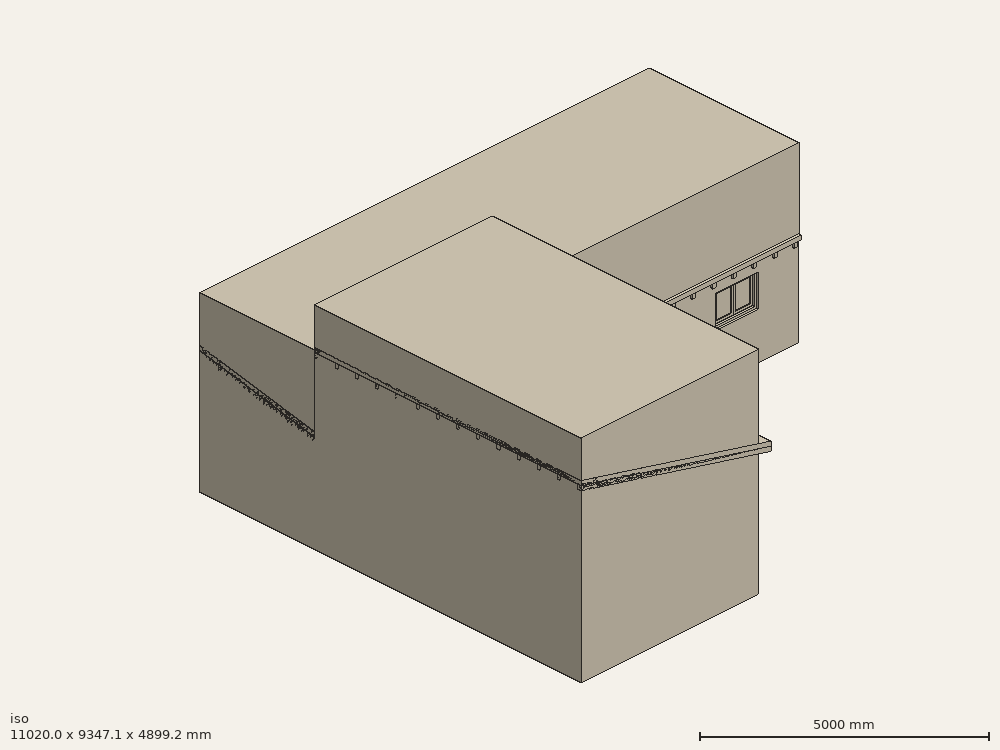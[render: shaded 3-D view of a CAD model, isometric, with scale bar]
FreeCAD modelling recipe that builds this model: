
FCSTD DOCUMENT  (FreeCAD 0.16R5653 (Git))
Label: Maison
License: All rights reserved
LicenseURL: http://en.wikipedia.org/wiki/All_rights_reserved
objects: Part::FeaturePython×87, Part::Part2DObjectPython×74, Sketcher::SketchObject×24, Part::Feature×17, Part::Extrusion×17, Part::MultiCommon×10, Part::Box×8, App::DocumentObjectGroupPython×5, App::DocumentObjectGroup×3, Part::Cut×2, App::FeaturePython×2, Part::Sweep×1, Part::Cylinder×1, Mesh::Feature×1, Mesh::FeaturePython×1
note: 243 computed .brp shape members not serialized (recipe doc carries the construction recipe); baked Part::Feature solids carry a one-line shape summary decoded from their .brp

FEATURE [Sketcher::SketchObject] Sketch001
  expr: Constraints[116] = Constraints.Cloison
  expr: Constraints[118] = Constraints.Cloison
  expr: Constraints[107] = Constraints.Cloison
  expr: Constraints[60] = Constraints.Cloison
  expr: Constraints[105] = Constraints.Cloison
  expr: Constraints[91] = Constraints.Cloison
  expr: Constraints[74] = Constraints.Cloison
  expr: Constraints[75] = Constraints.Cloison
  expr: Constraints[61] = Constraints.Cloison
  sketch-geometry (35):
    g0: LineSegment StartX=200 StartY=9007.1 StartZ=0 EndX=200 EndY=200 EndZ=0
    g1: LineSegment StartX=200 StartY=200 StartZ=0 EndX=4020 EndY=200 EndZ=0
    g2: LineSegment StartX=4020 StartY=200 StartZ=0 EndX=4020 EndY=5877.1 EndZ=0
    g3: LineSegment StartX=4020 StartY=5877.1 StartZ=0 EndX=10680 EndY=5877.1 EndZ=0
    g4: LineSegment StartX=10680 StartY=5877.1 StartZ=0 EndX=10680 EndY=9007.1 EndZ=0
    g5: LineSegment StartX=10680 StartY=9007.1 StartZ=0 EndX=200 EndY=9007.1 EndZ=0
    g6: LineSegment StartX=7960 StartY=5877.1 StartZ=0 EndX=7960 EndY=9007.1 EndZ=0
    g7: LineSegment StartX=7960 StartY=8107.1 StartZ=0 EndX=4020 EndY=8107.1 EndZ=0
    g8: LineSegment StartX=4020 StartY=8107.1 StartZ=0 EndX=4020 EndY=5877.1 EndZ=0
    g9: LineSegment StartX=3090 StartY=9007.1 StartZ=0 EndX=3090 EndY=7247.1 EndZ=0
    g10: LineSegment StartX=3090 StartY=7247.1 StartZ=0 EndX=200 EndY=7247.1 EndZ=0
    g11: LineSegment StartX=5140 StartY=8107.1 StartZ=0 EndX=5140 EndY=5877.1 EndZ=0
    g12: LineSegment StartX=4020 StartY=7327.1 StartZ=0 EndX=5140 EndY=7327.1 EndZ=0
    g13: LineSegment StartX=4580 StartY=8037.1 StartZ=0 EndX=4580 EndY=7327.1 EndZ=0
    g14: LineSegment StartX=4650 StartY=8037.1 StartZ=0 EndX=4650 EndY=7327.1 EndZ=0
    g15: LineSegment StartX=5210 StartY=8107.1 StartZ=0 EndX=5210 EndY=5877.1 EndZ=0
    g16: LineSegment StartX=8030 StartY=9007.1 StartZ=0 EndX=8030 EndY=5877.1 EndZ=0
    g17: LineSegment StartX=4020 StartY=8037.1 StartZ=0 EndX=5140 EndY=8037.1 EndZ=0
    g18: LineSegment StartX=200 StartY=5090 StartZ=0 EndX=2110 EndY=5090 EndZ=0
    g19: LineSegment StartX=2110 StartY=5090 StartZ=0 EndX=2560 EndY=5810 EndZ=0
    g20: LineSegment StartX=4090 StartY=7257.1 StartZ=0 EndX=5140 EndY=7257.1 EndZ=0
    g21: LineSegment StartX=4330 StartY=5877.1 StartZ=0 EndX=4330 EndY=6557.1 EndZ=0
    g22: LineSegment StartX=4330 StartY=6557.1 StartZ=0 EndX=4090 EndY=6557.1 EndZ=0
    g23: LineSegment StartX=4090 StartY=6557.1 StartZ=0 EndX=4090 EndY=7257.1 EndZ=0
    g24: LineSegment StartX=4090 StartY=7327.1 StartZ=0 EndX=4090 EndY=8037.1 EndZ=0
    g25: LineSegment StartX=5210 StartY=8037.1 StartZ=0 EndX=7960 EndY=8037.1 EndZ=0
    g26: LineSegment StartX=3160 StartY=9007.1 StartZ=0 EndX=3160 EndY=6307.1 EndZ=0
    g27: LineSegment StartX=3160 StartY=6307.1 StartZ=0 EndX=3090 EndY=6307.1 EndZ=0
    g28: LineSegment StartX=3090 StartY=6307.1 StartZ=0 EndX=3090 EndY=7177.1 EndZ=0
    g29: LineSegment StartX=3090 StartY=7177.1 StartZ=0 EndX=200 EndY=7177.1 EndZ=0
    g30: LineSegment StartX=1520 StartY=7247.1 StartZ=0 EndX=1520 EndY=9007.1 EndZ=0
    g31: LineSegment StartX=1590 StartY=7247.1 StartZ=0 EndX=1590 EndY=9007.1 EndZ=0
    g32: LineSegment StartX=200 StartY=5160 StartZ=0 EndX=2071.2 EndY=5160 EndZ=0
    g33: LineSegment StartX=2071.2 StartY=5160 StartZ=0 EndX=2500.64 EndY=5847.1 EndZ=0
    g34: LineSegment StartX=2500.64 StartY=5847.1 StartZ=0 EndX=2560 EndY=5810 EndZ=0
  constraints (123):
    c: Vertical(g0)
    c: Coincident(g0,g1)
    c: Horizontal(g1)
    c: Coincident(g1,g2)
    c: Vertical(g2)
    c: Coincident(g2,g3)
    c: Horizontal(g3)
    c: Coincident(g3,g4)
    c: Vertical(g4)
    c: Coincident(g4,g5)
    c: Coincident(g5,g0)
    c: Horizontal(g5)
    c: PointOnObject(g6,g3)
    c: PointOnObject(g6,g5)
    c: Vertical(g6)
    c: PointOnObject(g7,g6)
    c: Horizontal(g7)
    c: Coincident(g8,g7)
    c: Vertical(g8)
    c: Coincident(g8,g2)
    c: PointOnObject(g9,g5)
    c: Vertical(g9)
    c: Coincident(g9,g10)
    c: PointOnObject(g10,g0)
    c: Horizontal(g10)
    c: PointOnObject(g11,g7)
    c: PointOnObject(g11,g3)
    c: Vertical(g11)
    c: PointOnObject(g12,g8)
    c: PointOnObject(g12,g11)
    c: Horizontal(g12)
    c: PointOnObject(g13,g12)
    c: Vertical(g13)
    c: PointOnObject(g14,g12)
    c: Vertical(g14)
    c: PointOnObject(g15,g7)
    c: PointOnObject(g15,g3)
    c: Vertical(g15)
    c: PointOnObject(g16,g5)
    c: PointOnObject(g16,g3)
    c: Vertical(g16)
    c: PointOnObject(g17,g8)
    c: PointOnObject(g17,g11)
    c: Horizontal(g17)
    c: PointOnObject(g13,g17)
    c: PointOnObject(g14,g17)
    c: DistanceX(g1) = 3820
    c: PointOnObject(g18,g0)
    c: Horizontal(g18)
    c: Coincident(g18,g19)
    c: DistanceX(g18) = 1910
    c: DistanceX(g19) = 450
    c: DistanceY(g19) = 720
    c: DistanceY(g0,g18) = 4890
    c: DistanceX(g16,g4) = 2650
    c: DistanceY(g4) = 3130
    c: DistanceY(g6,g7) = -900
    c: DistanceX(g6,g16) = 70  'Cloison'
    c: DistanceX(g15,g7) = 2750
    c: DistanceX(g11,g15) = 70
    c: DistanceY(g17,g7) = 70
    c: DistanceX(g13,g14) = 70
    c: PointOnObject(g20,g11)
    c: Horizontal(g20)
    c: DistanceX(g20) = 1050
    c: PointOnObject(g21,g3)
    c: Vertical(g21)
    c: DistanceX(g21,g11) = 810
    c: DistanceY(g13) = -710
    c: Coincident(g21,g22)
    c: Horizontal(g22)
    c: Coincident(g22,g23)
    c: Coincident(g23,g20)
    c: Vertical(g23)
    c: DistanceX(g12,g20) = 70
    c: DistanceY(g20,g12) = 70
    c: DistanceY(g21,g21) = 680
    c: PointOnObject(g24,g12)
    c: PointOnObject(g24,g17)
    c: Vertical(g24)
    c: PointOnObject(g24,g23)
    c: DistanceX(g24,g17) = 1050
    c: DistanceX(g14,g17) = 490
    c: DistanceX(g24,g13) = 490
    c: PointOnObject(g25,g15)
    c: PointOnObject(g25,g6)
    c: Horizontal(g25)
    c: PointOnObject(g25,g17)
    c: PointOnObject(g26,g5)
    c: Vertical(g26)
    c: DistanceX(g26,g7) = 860
    c: DistanceX(g9,g26) = 70
    c: Coincident(g26,g27)
    c: Horizontal(g27)
    c: Coincident(g27,g28)
    c: Vertical(g28)
    c: Coincident(g28,g29)
    c: PointOnObject(g29,g0)
    c: Horizontal(g29)
    c: PointOnObject(g30,g10)
    c: PointOnObject(g30,g5)
    c: PointOnObject(g31,g10)
    c: PointOnObject(g31,g5)
    c: Vertical(g31)
    c: Vertical(g30)
    c: DistanceX(g30,g31) = 70
    c: PointOnObject(g28,g9)
    c: DistanceY(g29,g10) = 70
    c: DistanceY(g9,g9) = 1760
    c: DistanceX(g31,g9) = 1500
    c: DistanceY(g27,g28) = 870
    c: PointOnObject(g32,g0)
    c: Horizontal(g32)
    c: Coincident(g32,g33)
    c: Coincident(g33,g34)
    c: Coincident(g34,g19)
    c: Distance(g34) = 70
    c: Parallel(g33,g19)
    c: DistanceY(g18,g32) = 70
    c: Perpendicular(g34,g19)
    c: DistanceX(g0) = 200
    c: DistanceY(g0) = 200
    c: DistanceY(g33,g27) = 460
FEATURE [Sketcher::SketchObject] TraceDuMur
  sketch-geometry (1):
    g0: LineSegment StartX=8030 StartY=5877.1 StartZ=0 EndX=8030 EndY=9007.1 EndZ=0
FEATURE [Sketcher::SketchObject] TraceDuMur001
  sketch-geometry (1):
    g0: LineSegment StartX=7960 StartY=8037.1 StartZ=0 EndX=4020 EndY=8037.1 EndZ=0
FEATURE [Part::FeaturePython] Wall001  label="Cloison"  # WARN: FeaturePython — macro-defined, semantics opaque (R4)
  Align = 0
  Base = -> TraceDuMur001
  Face = 0
  Height = 3000
  Length = 0
  MoveWithHost = false
  Normal = (0,0,0)
  Role = 0
  Width = 70
FEATURE [Sketcher::SketchObject] TraceDuMur002
  sketch-geometry (1):
    g0: LineSegment StartX=5210 StartY=8037.1 StartZ=0 EndX=5210 EndY=5877.1 EndZ=0
FEATURE [Part::FeaturePython] Wall002  label="Cloison001"  # WARN: FeaturePython — macro-defined, semantics opaque (R4)
  Align = 0
  Base = -> TraceDuMur002
  Face = 0
  Height = 3000
  Length = 0
  MoveWithHost = false
  Normal = (0,0,0)
  Role = 0
  Width = 70
FEATURE [Sketcher::SketchObject] TraceDuMur003
  sketch-geometry (1):
    g0: LineSegment StartX=4090 StartY=8037.1 StartZ=0 EndX=4090 EndY=6557.1 EndZ=0
FEATURE [Part::FeaturePython] Wall003  label="Cloison004"  # WARN: FeaturePython — macro-defined, semantics opaque (R4)
  Align = 0
  Base = -> TraceDuMur003
  Face = 0
  Height = 3000
  Length = 0
  MoveWithHost = false
  Normal = (0,0,0)
  Role = 0
  Width = 70
FEATURE [Sketcher::SketchObject] TraceDuMur004
  sketch-geometry (1):
    g0: LineSegment StartX=4650 StartY=8037.1 StartZ=0 EndX=4650 EndY=7327.1 EndZ=0
FEATURE [Part::FeaturePython] Wall004  label="Cloison003"  # WARN: FeaturePython — macro-defined, semantics opaque (R4)
  Align = 0
  Base = -> TraceDuMur004
  Face = 0
  Height = 3000
  Length = 0
  MoveWithHost = false
  Normal = (0,0,0)
  Role = 0
  Width = 70
FEATURE [Sketcher::SketchObject] TraceDuMur005
  sketch-geometry (1):
    g0: LineSegment StartX=5140 StartY=7257.1 StartZ=0 EndX=4090 EndY=7257.1 EndZ=0
FEATURE [Part::FeaturePython] Wall005  label="Cloison002"  # WARN: FeaturePython — macro-defined, semantics opaque (R4)
  Align = 0
  Base = -> TraceDuMur005
  Face = 0
  Height = 3000
  Length = 0
  MoveWithHost = false
  Normal = (0,0,0)
  Role = 0
  Width = 70
FEATURE [Part::Part2DObjectPython] Line  # Draft 2D object (typed FeaturePython)
  ChamferSize = 0
  Closed = false
  End = (3160,6307.1,0)
  FilletRadius = 0
  Length = 2700
  MakeFace = false
  Points = (2) [(3160,9007.1,0),(3160,6307.1,0)]
  Start = (3160,9007.1,0)
FEATURE [Part::Part2DObjectPython] Line001  # Draft 2D object (typed FeaturePython)
  ChamferSize = 0
  Closed = false
  End = (200,7177.1,0)
  FilletRadius = 0
  Length = 2890
  MakeFace = false
  Points = (2) [(3090,7177.1,0),(200,7177.1,0)]
  Start = (3090,7177.1,0)
FEATURE [Part::Part2DObjectPython] Line002  # Draft 2D object (typed FeaturePython)
  ChamferSize = 0
  Closed = false
  End = (1590,7247.1,0)
  FilletRadius = 0
  Length = 1760
  MakeFace = false
  Points = (2) [(1590,9007.1,0),(1590,7247.1,0)]
  Start = (1590,9007.1,0)
FEATURE [Part::FeaturePython] Wall007  label="Cloison005"  # WARN: FeaturePython — macro-defined, semantics opaque (R4)
  Align = 0
  Base = -> Line001
  Face = 0
  Height = 3000
  Length = 0
  MoveWithHost = false
  Normal = (0,0,0)
  Role = 0
  Width = 70
FEATURE [Part::FeaturePython] Wall008  label="Cloison006"  # WARN: FeaturePython — macro-defined, semantics opaque (R4)
  Align = 0
  Base = -> Line002
  Face = 0
  Height = 3000
  Length = 0
  MoveWithHost = false
  Normal = (0,0,0)
  Role = 0
  Width = 70
FEATURE [Part::Part2DObjectPython] DWire  # Draft 2D object (typed FeaturePython)
  ChamferSize = 0
  Closed = true
  End = (200,9007.1,0)
  FilletRadius = 0
  Length = 38574.2
  MakeFace = false
  Points = (6) [(200,200,0),(4020,200,0),(4020,5877.1,0),(10680,5877.1,0),(10680,9007.1,0),(200,9007.1,0)]
  Start = (200,200,0)
FEATURE [Part::Part2DObjectPython] Line003  # Draft 2D object (typed FeaturePython)
  ChamferSize = 0
  Closed = false
  End = (4020,6557.1,0)
  FilletRadius = 0
  Length = 680
  MakeFace = false
  Points = (2) [(4020,5877.1,0),(4020,6557.1,0)]
  Start = (4020,5877.1,0)
FEATURE [Part::Part2DObjectPython] DWire001  # Draft 2D object (typed FeaturePython)
  ChamferSize = 0
  Closed = false
  End = (2560,5810,0)
  FilletRadius = 0
  Length = 2759.06
  MakeFace = false
  Points = (3) [(200,5090,0),(2110,5090,0),(2560,5810,0)]
  Start = (200,5090,0)
FEATURE [Sketcher::SketchObject] Sketch
  Placement = pos=(4290,4307,30) rot=(0.57735,0.57735,0.57735;2.0944rad)
  sketch-geometry (12):
    g0: LineSegment StartX=0 StartY=0 StartZ=0 EndX=900 EndY=0 EndZ=0
    g1: LineSegment StartX=900 StartY=0 StartZ=0 EndX=900 EndY=2150 EndZ=0
    g2: LineSegment StartX=900 StartY=2150 StartZ=0 EndX=0 EndY=2150 EndZ=0
    g3: LineSegment StartX=0 StartY=2150 StartZ=0 EndX=0 EndY=0 EndZ=0
    g4: LineSegment StartX=50 StartY=0 StartZ=0 EndX=850 EndY=0 EndZ=0
    g5: LineSegment StartX=850 StartY=0 StartZ=0 EndX=850 EndY=2100 EndZ=0
    g6: LineSegment StartX=850 StartY=2100 StartZ=0 EndX=50 EndY=2100 EndZ=0
    g7: LineSegment StartX=50 StartY=2100 StartZ=0 EndX=50 EndY=0 EndZ=0
    g8: LineSegment StartX=100 StartY=2050 StartZ=0 EndX=800 EndY=2050 EndZ=0
    g9: LineSegment StartX=800 StartY=2050 StartZ=0 EndX=800 EndY=1200 EndZ=0
    g10: LineSegment StartX=800 StartY=1200 StartZ=0 EndX=100 EndY=1200 EndZ=0
    g11: LineSegment StartX=100 StartY=1200 StartZ=0 EndX=100 EndY=2050 EndZ=0
  constraints (35):
    c: Coincident(g0,g1)
    c: Coincident(g1,g2)
    c: Coincident(g2,g3)
    c: Coincident(g3,g0)
    c: Horizontal(g0)
    c: Horizontal(g2)
    c: Vertical(g1)
    c: Vertical(g3)
    c: Coincident(g4,g5)
    c: Coincident(g5,g6)
    c: Coincident(g6,g7)
    c: Coincident(g7,g4)
    c: Horizontal(g4)
    c: Horizontal(g6)
    c: Vertical(g5)
    c: Vertical(g7)
    c: DistanceY(g1) = 2150
    c: DistanceX(g0) = 900
    c: DistanceY(g6,g2) = 50
    c: DistanceX(g2,g6) = 50
    c: DistanceX(g4,g0) = 50
    c: DistanceY(g0,g4) = 0
    c: Coincident(g0,g-1)
    c: Coincident(g8,g9)
    c: Coincident(g9,g10)
    c: Coincident(g10,g11)
    c: Coincident(g11,g8)
    c: Horizontal(g8)
    c: Horizontal(g10)
    c: Vertical(g9)
    c: Vertical(g11)
    c: DistanceX(g6,g8) = 50
    c: DistanceY(g8,g6) = 50
    c: DistanceX(g8,g5) = 50
    c: DistanceY(g10,g8) = 850
FEATURE [Part::FeaturePython] Window  label="Porte d'entrée"  # WARN: FeaturePython — macro-defined, semantics opaque (R4)
  Base = -> Sketch
  Height = 2150
  HoleDepth = 0
  MoveWithHost = true
  Normal = (-1,0,0)
  Preset = 6
  Role = 1
  Width = 900
  WindowParts = OuterFrame | Frame | Wire0,Wire1 | 50.0 | 50.0 | Door | Solid panel | Wire2,Wire1 | 50.0 | 100.0 | Vitrage | Glass panel | Wire2 | 12.0 | 125.0
FEATURE [Sketcher::SketchObject] Sketch002
  Placement = pos=(4290,1150,900) rot=(0.57735,0.57735,0.57735;2.0944rad)
  sketch-geometry (24):
    g0: LineSegment StartX=0 StartY=0 StartZ=0 EndX=900 EndY=0 EndZ=0
    g1: LineSegment StartX=900 StartY=0 StartZ=0 EndX=900 EndY=1780 EndZ=0
    g2: LineSegment StartX=900 StartY=1780 StartZ=0 EndX=0 EndY=1780 EndZ=0
    g3: LineSegment StartX=0 StartY=1780 StartZ=0 EndX=0 EndY=0 EndZ=0
    g4: LineSegment StartX=50 StartY=50 StartZ=0 EndX=850 EndY=50 EndZ=0
    g5: LineSegment StartX=850 StartY=50 StartZ=0 EndX=850 EndY=1730 EndZ=0
    g6: LineSegment StartX=850 StartY=1730 StartZ=0 EndX=50 EndY=1730 EndZ=0
    g7: LineSegment StartX=50 StartY=1730 StartZ=0 EndX=50 EndY=50 EndZ=0
    g8: LineSegment StartX=55 StartY=55 StartZ=0 EndX=447.5 EndY=55 EndZ=0
    g9: LineSegment StartX=447.5 StartY=55 StartZ=0 EndX=447.5 EndY=1725 EndZ=0
    g10: LineSegment StartX=447.5 StartY=1725 StartZ=0 EndX=55 EndY=1725 EndZ=0
    g11: LineSegment StartX=55 StartY=1725 StartZ=0 EndX=55 EndY=55 EndZ=0
    g12: LineSegment StartX=105 StartY=105 StartZ=0 EndX=397.5 EndY=105 EndZ=0
    g13: LineSegment StartX=397.5 StartY=105 StartZ=0 EndX=397.5 EndY=1675 EndZ=0
    g14: LineSegment StartX=397.5 StartY=1675 StartZ=0 EndX=105 EndY=1675 EndZ=0
    g15: LineSegment StartX=105 StartY=1675 StartZ=0 EndX=105 EndY=105 EndZ=0
    g16: LineSegment StartX=452.5 StartY=55 StartZ=0 EndX=845 EndY=55 EndZ=0
    g17: LineSegment StartX=845 StartY=55 StartZ=0 EndX=845 EndY=1725 EndZ=0
    g18: LineSegment StartX=845 StartY=1725 StartZ=0 EndX=452.5 EndY=1725 EndZ=0
    g19: LineSegment StartX=452.5 StartY=1725 StartZ=0 EndX=452.5 EndY=55 EndZ=0
    g20: LineSegment StartX=502.5 StartY=105 StartZ=0 EndX=795 EndY=105 EndZ=0
    g21: LineSegment StartX=795 StartY=105 StartZ=0 EndX=795 EndY=1675 EndZ=0
    g22: LineSegment StartX=795 StartY=1675 StartZ=0 EndX=502.5 EndY=1675 EndZ=0
    g23: LineSegment StartX=502.5 StartY=1675 StartZ=0 EndX=502.5 EndY=105 EndZ=0
  constraints (71):
    c: Coincident(g0,g1)
    c: Coincident(g1,g2)
    c: Coincident(g2,g3)
    c: Coincident(g3,g0)
    c: Horizontal(g0)
    c: Horizontal(g2)
    c: Vertical(g1)
    c: Vertical(g3)
    c: Coincident(g4,g5)
    c: Coincident(g5,g6)
    c: Coincident(g6,g7)
    c: Coincident(g7,g4)
    c: Horizontal(g4)
    c: Horizontal(g6)
    c: Vertical(g5)
    c: Vertical(g7)
    c: DistanceY(g1) = 1780
    c: DistanceX(g0) = 900
    c: DistanceY(g6,g2) = 50
    c: DistanceX(g2,g6) = 50
    c: DistanceX(g4,g0) = 50
    c: DistanceY(g0,g4) = 50
    c: Coincident(g0,g-1)
    c: Coincident(g8,g9)
    c: Coincident(g9,g10)
    c: Coincident(g10,g11)
    c: Coincident(g11,g8)
    c: Horizontal(g8)
    c: Horizontal(g10)
    c: Vertical(g9)
    c: Vertical(g11)
    c: Coincident(g12,g13)
    c: Coincident(g13,g14)
    c: Coincident(g14,g15)
    c: Coincident(g15,g12)
    c: Horizontal(g12)
    c: Horizontal(g14)
    c: Vertical(g13)
    c: Vertical(g15)
    c: Coincident(g16,g17)
    c: Coincident(g17,g18)
    c: Coincident(g18,g19)
    c: Coincident(g19,g16)
    c: Horizontal(g16)
    c: Horizontal(g18)
    c: Vertical(g17)
    c: Vertical(g19)
    c: Coincident(g20,g21)
    c: Coincident(g21,g22)
    c: Coincident(g22,g23)
    c: Coincident(g23,g20)
    c: Horizontal(g20)
    c: Horizontal(g22)
    c: Vertical(g21)
    c: Vertical(g23)
    c: DistanceY(g8,g12) = 50
    c: DistanceX(g8,g12) = 50
    c: DistanceX(g21,g17) = 50
    c: DistanceY(g21,g17) = 50
    c: DistanceX(g16,g20) = 50
    c: DistanceX(g14,g10) = 50
    c: Equal(g22,g14)
    c: DistanceY(g8,g16) = 0
    c: DistanceY(g10,g18) = 0
    c: DistanceX(g4,g8) = 5
    c: DistanceY(g4,g8) = 5
    c: DistanceX(g6,g18) = -5
    c: DistanceY(g6,g18) = -5
    c: DistanceX(g9,g19) = 5
    c: PointOnObject(g13,g22)
    c: PointOnObject(g20,g12)
FEATURE [Part::FeaturePython] Window001  label="Fenêtre Salon"  # WARN: FeaturePython — macro-defined, semantics opaque (R4)
  Base = -> Sketch002
  Height = 1780
  HoleDepth = 0
  MoveWithHost = true
  Normal = (-1,0,0)
  Preset = 3
  Role = 0
  Width = 900
  WindowParts = OuterFrame | Frame | Wire0,Wire1 | 50.0 | 50.0 | LeftFrame | Frame | Wire2,Wire3 | 50.0 | 100.0 | LeftGlass | Glass panel | Wire3 | 5.0 | 125.0 | RightFrame | Frame | Wire4,Wire5 | 50.0 | 100.0 | RightGlass | Glass panel | Wire5 | 5.0 | 125.0
FEATURE [Sketcher::SketchObject] Sketch003
  Placement = pos=(4450.48,5607.1,1350) rot=(1,0,0;1.5708rad)
  sketch-geometry (16):
    g0: LineSegment StartX=0 StartY=0 StartZ=0 EndX=400 EndY=0 EndZ=0
    g1: LineSegment StartX=400 StartY=0 StartZ=0 EndX=400 EndY=400 EndZ=0
    g2: LineSegment StartX=400 StartY=400 StartZ=0 EndX=0 EndY=400 EndZ=0
    g3: LineSegment StartX=0 StartY=400 StartZ=0 EndX=0 EndY=0 EndZ=0
    g4: LineSegment StartX=50 StartY=50 StartZ=0 EndX=350 EndY=50 EndZ=0
    g5: LineSegment StartX=350 StartY=50 StartZ=0 EndX=350 EndY=350 EndZ=0
    g6: LineSegment StartX=350 StartY=350 StartZ=0 EndX=50 EndY=350 EndZ=0
    g7: LineSegment StartX=50 StartY=350 StartZ=0 EndX=50 EndY=50 EndZ=0
    g8: LineSegment StartX=55 StartY=55 StartZ=0 EndX=345 EndY=55 EndZ=0
    g9: LineSegment StartX=345 StartY=55 StartZ=0 EndX=345 EndY=345 EndZ=0
    g10: LineSegment StartX=345 StartY=345 StartZ=0 EndX=55 EndY=345 EndZ=0
    g11: LineSegment StartX=55 StartY=345 StartZ=0 EndX=55 EndY=55 EndZ=0
    g12: LineSegment StartX=105 StartY=105 StartZ=0 EndX=295 EndY=105 EndZ=0
    g13: LineSegment StartX=295 StartY=105 StartZ=0 EndX=295 EndY=295 EndZ=0
    g14: LineSegment StartX=295 StartY=295 StartZ=0 EndX=105 EndY=295 EndZ=0
    g15: LineSegment StartX=105 StartY=295 StartZ=0 EndX=105 EndY=105 EndZ=0
  constraints (47):
    c: Coincident(g0,g1)
    c: Coincident(g1,g2)
    c: Coincident(g2,g3)
    c: Coincident(g3,g0)
    c: Horizontal(g0)
    c: Horizontal(g2)
    c: Vertical(g1)
    c: Vertical(g3)
    c: Coincident(g4,g5)
    c: Coincident(g5,g6)
    c: Coincident(g6,g7)
    c: Coincident(g7,g4)
    c: Horizontal(g4)
    c: Horizontal(g6)
    c: Vertical(g5)
    c: Vertical(g7)
    c: DistanceY(g1) = 400
    c: DistanceX(g0) = 400
    c: DistanceY(g6,g2) = 50
    c: DistanceX(g2,g6) = 50
    c: DistanceX(g4,g0) = 50
    c: DistanceY(g0,g4) = 50
    c: Coincident(g0,g-1)
    c: Coincident(g8,g9)
    c: Coincident(g9,g10)
    c: Coincident(g10,g11)
    c: Coincident(g11,g8)
    c: Horizontal(g8)
    c: Horizontal(g10)
    c: Vertical(g9)
    c: Vertical(g11)
    c: Coincident(g12,g13)
    c: Coincident(g13,g14)
    c: Coincident(g14,g15)
    c: Coincident(g15,g12)
    c: Horizontal(g12)
    c: Horizontal(g14)
    c: Vertical(g13)
    c: Vertical(g15)
    c: DistanceX(g8,g12) = 50
    c: DistanceY(g8,g12) = 50
    c: DistanceX(g14,g10) = 50
    c: DistanceY(g14,g10) = 50
    c: DistanceX(g4,g8) = 5
    c: DistanceY(g4,g8) = 5
    c: DistanceX(g10,g6) = 5
    c: DistanceY(g10,g6) = 5
FEATURE [Part::FeaturePython] Window002  label="Fenêtre WC"  # WARN: FeaturePython — macro-defined, semantics opaque (R4)
  Base = -> Sketch003
  Height = 400
  HoleDepth = 0
  MoveWithHost = true
  Normal = (0,1,0)
  Preset = 2
  Role = 0
  Width = 400
  WindowParts = OuterFrame | Frame | Wire0,Wire1 | 50.0 | 50.0 | InnerFrame | Frame | Wire2,Wire3 | 50.0 | 100.0 | InnerGlass | Glass panel | Wire3 | 5.0 | 125.0
FEATURE [Sketcher::SketchObject] Sketch004
  Placement = pos=(5914.63,5607.1,1070) rot=(1,0,0;1.5708rad)
  sketch-geometry (24):
    g0: LineSegment StartX=0 StartY=0 StartZ=0 EndX=1050 EndY=0 EndZ=0
    g1: LineSegment StartX=1050 StartY=0 StartZ=0 EndX=1050 EndY=750 EndZ=0
    g2: LineSegment StartX=1050 StartY=750 StartZ=0 EndX=0 EndY=750 EndZ=0
    g3: LineSegment StartX=0 StartY=750 StartZ=0 EndX=0 EndY=0 EndZ=0
    g4: LineSegment StartX=50 StartY=50 StartZ=0 EndX=1000 EndY=50 EndZ=0
    g5: LineSegment StartX=1000 StartY=50 StartZ=0 EndX=1000 EndY=700 EndZ=0
    g6: LineSegment StartX=1000 StartY=700 StartZ=0 EndX=50 EndY=700 EndZ=0
    g7: LineSegment StartX=50 StartY=700 StartZ=0 EndX=50 EndY=50 EndZ=0
    g8: LineSegment StartX=55 StartY=55 StartZ=0 EndX=522.5 EndY=55 EndZ=0
    g9: LineSegment StartX=522.5 StartY=55 StartZ=0 EndX=522.5 EndY=695 EndZ=0
    g10: LineSegment StartX=522.5 StartY=695 StartZ=0 EndX=55 EndY=695 EndZ=0
    g11: LineSegment StartX=55 StartY=695 StartZ=0 EndX=55 EndY=55 EndZ=0
    g12: LineSegment StartX=105 StartY=105 StartZ=0 EndX=472.5 EndY=105 EndZ=0
    g13: LineSegment StartX=472.5 StartY=105 StartZ=0 EndX=472.5 EndY=645 EndZ=0
    g14: LineSegment StartX=472.5 StartY=645 StartZ=0 EndX=105 EndY=645 EndZ=0
    g15: LineSegment StartX=105 StartY=645 StartZ=0 EndX=105 EndY=105 EndZ=0
    g16: LineSegment StartX=527.5 StartY=55 StartZ=0 EndX=995 EndY=55 EndZ=0
    g17: LineSegment StartX=995 StartY=55 StartZ=0 EndX=995 EndY=695 EndZ=0
    g18: LineSegment StartX=995 StartY=695 StartZ=0 EndX=527.5 EndY=695 EndZ=0
    g19: LineSegment StartX=527.5 StartY=695 StartZ=0 EndX=527.5 EndY=55 EndZ=0
    g20: LineSegment StartX=577.5 StartY=105 StartZ=0 EndX=945 EndY=105 EndZ=0
    g21: LineSegment StartX=945 StartY=105 StartZ=0 EndX=945 EndY=645 EndZ=0
    g22: LineSegment StartX=945 StartY=645 StartZ=0 EndX=577.5 EndY=645 EndZ=0
    g23: LineSegment StartX=577.5 StartY=645 StartZ=0 EndX=577.5 EndY=105 EndZ=0
  constraints (71):
    c: Coincident(g0,g1)
    c: Coincident(g1,g2)
    c: Coincident(g2,g3)
    c: Coincident(g3,g0)
    c: Horizontal(g0)
    c: Horizontal(g2)
    c: Vertical(g1)
    c: Vertical(g3)
    c: Coincident(g4,g5)
    c: Coincident(g5,g6)
    c: Coincident(g6,g7)
    c: Coincident(g7,g4)
    c: Horizontal(g4)
    c: Horizontal(g6)
    c: Vertical(g5)
    c: Vertical(g7)
    c: DistanceY(g1) = 750
    c: DistanceX(g0) = 1050
    c: DistanceY(g6,g2) = 50
    c: DistanceX(g2,g6) = 50
    c: DistanceX(g4,g0) = 50
    c: DistanceY(g0,g4) = 50
    c: Coincident(g0,g-1)
    c: Coincident(g8,g9)
    c: Coincident(g9,g10)
    c: Coincident(g10,g11)
    c: Coincident(g11,g8)
    c: Horizontal(g8)
    c: Horizontal(g10)
    c: Vertical(g9)
    c: Vertical(g11)
    c: Coincident(g12,g13)
    c: Coincident(g13,g14)
    c: Coincident(g14,g15)
    c: Coincident(g15,g12)
    c: Horizontal(g12)
    c: Horizontal(g14)
    c: Vertical(g13)
    c: Vertical(g15)
    c: Coincident(g16,g17)
    c: Coincident(g17,g18)
    c: Coincident(g18,g19)
    c: Coincident(g19,g16)
    c: Horizontal(g16)
    c: Horizontal(g18)
    c: Vertical(g17)
    c: Vertical(g19)
    c: Coincident(g20,g21)
    c: Coincident(g21,g22)
    c: Coincident(g22,g23)
    c: Coincident(g23,g20)
    c: Horizontal(g20)
    c: Horizontal(g22)
    c: Vertical(g21)
    c: Vertical(g23)
    c: DistanceY(g8,g12) = 50
    c: DistanceX(g8,g12) = 50
    c: DistanceX(g21,g17) = 50
    c: DistanceY(g21,g17) = 50
    c: DistanceX(g16,g20) = 50
    c: DistanceX(g14,g10) = 50
    c: Equal(g22,g14)
    c: DistanceY(g8,g16) = 0
    c: DistanceY(g10,g18) = 0
    c: DistanceX(g4,g8) = 5
    c: DistanceY(g4,g8) = 5
    c: DistanceX(g6,g18) = -5
    c: DistanceY(g6,g18) = -5
    c: DistanceX(g9,g19) = 5
    c: PointOnObject(g13,g22)
    c: PointOnObject(g20,g12)
FEATURE [Part::FeaturePython] Window003  label="Fenêtre Bureau"  # WARN: FeaturePython — macro-defined, semantics opaque (R4)
  Base = -> Sketch004
  Height = 750
  HoleDepth = 0
  MoveWithHost = true
  Normal = (0,1,0)
  Preset = 3
  Role = 0
  Width = 1050
  WindowParts = <same value as first occurrence — deduplicated (x3 in doc)>
FEATURE [Sketcher::SketchObject] Sketch005
  Placement = pos=(8914.63,5607.1,1070) rot=(1,0,0;1.5708rad)
  sketch-geometry (24):
    g0: LineSegment StartX=0 StartY=0 StartZ=0 EndX=1050 EndY=0 EndZ=0
    g1: LineSegment StartX=1050 StartY=0 StartZ=0 EndX=1050 EndY=750 EndZ=0
    g2: LineSegment StartX=1050 StartY=750 StartZ=0 EndX=0 EndY=750 EndZ=0
    g3: LineSegment StartX=0 StartY=750 StartZ=0 EndX=0 EndY=0 EndZ=0
    g4: LineSegment StartX=50 StartY=50 StartZ=0 EndX=1000 EndY=50 EndZ=0
    g5: LineSegment StartX=1000 StartY=50 StartZ=0 EndX=1000 EndY=700 EndZ=0
    g6: LineSegment StartX=1000 StartY=700 StartZ=0 EndX=50 EndY=700 EndZ=0
    g7: LineSegment StartX=50 StartY=700 StartZ=0 EndX=50 EndY=50 EndZ=0
    g8: LineSegment StartX=55 StartY=55 StartZ=0 EndX=522.5 EndY=55 EndZ=0
    g9: LineSegment StartX=522.5 StartY=55 StartZ=0 EndX=522.5 EndY=695 EndZ=0
    g10: LineSegment StartX=522.5 StartY=695 StartZ=0 EndX=55 EndY=695 EndZ=0
    g11: LineSegment StartX=55 StartY=695 StartZ=0 EndX=55 EndY=55 EndZ=0
    g12: LineSegment StartX=105 StartY=105 StartZ=0 EndX=472.5 EndY=105 EndZ=0
    g13: LineSegment StartX=472.5 StartY=105 StartZ=0 EndX=472.5 EndY=645 EndZ=0
    g14: LineSegment StartX=472.5 StartY=645 StartZ=0 EndX=105 EndY=645 EndZ=0
    g15: LineSegment StartX=105 StartY=645 StartZ=0 EndX=105 EndY=105 EndZ=0
    g16: LineSegment StartX=527.5 StartY=55 StartZ=0 EndX=995 EndY=55 EndZ=0
    g17: LineSegment StartX=995 StartY=55 StartZ=0 EndX=995 EndY=695 EndZ=0
    g18: LineSegment StartX=995 StartY=695 StartZ=0 EndX=527.5 EndY=695 EndZ=0
    g19: LineSegment StartX=527.5 StartY=695 StartZ=0 EndX=527.5 EndY=55 EndZ=0
    g20: LineSegment StartX=577.5 StartY=105 StartZ=0 EndX=945 EndY=105 EndZ=0
    g21: LineSegment StartX=945 StartY=105 StartZ=0 EndX=945 EndY=645 EndZ=0
    g22: LineSegment StartX=945 StartY=645 StartZ=0 EndX=577.5 EndY=645 EndZ=0
    g23: LineSegment StartX=577.5 StartY=645 StartZ=0 EndX=577.5 EndY=105 EndZ=0
  constraints (71):
    c: Coincident(g0,g1)
    c: Coincident(g1,g2)
    c: Coincident(g2,g3)
    c: Coincident(g3,g0)
    c: Horizontal(g0)
    c: Horizontal(g2)
    c: Vertical(g1)
    c: Vertical(g3)
    c: Coincident(g4,g5)
    c: Coincident(g5,g6)
    c: Coincident(g6,g7)
    c: Coincident(g7,g4)
    c: Horizontal(g4)
    c: Horizontal(g6)
    c: Vertical(g5)
    c: Vertical(g7)
    c: DistanceY(g1) = 750
    c: DistanceX(g0) = 1050
    c: DistanceY(g6,g2) = 50
    c: DistanceX(g2,g6) = 50
    c: DistanceX(g4,g0) = 50
    c: DistanceY(g0,g4) = 50
    c: Coincident(g0,g-1)
    c: Coincident(g8,g9)
    c: Coincident(g9,g10)
    c: Coincident(g10,g11)
    c: Coincident(g11,g8)
    c: Horizontal(g8)
    c: Horizontal(g10)
    c: Vertical(g9)
    c: Vertical(g11)
    c: Coincident(g12,g13)
    c: Coincident(g13,g14)
    c: Coincident(g14,g15)
    c: Coincident(g15,g12)
    c: Horizontal(g12)
    c: Horizontal(g14)
    c: Vertical(g13)
    c: Vertical(g15)
    c: Coincident(g16,g17)
    c: Coincident(g17,g18)
    c: Coincident(g18,g19)
    c: Coincident(g19,g16)
    c: Horizontal(g16)
    c: Horizontal(g18)
    c: Vertical(g17)
    c: Vertical(g19)
    c: Coincident(g20,g21)
    c: Coincident(g21,g22)
    c: Coincident(g22,g23)
    c: Coincident(g23,g20)
    c: Horizontal(g20)
    c: Horizontal(g22)
    c: Vertical(g21)
    c: Vertical(g23)
    c: DistanceY(g8,g12) = 50
    c: DistanceX(g8,g12) = 50
    c: DistanceX(g21,g17) = 50
    c: DistanceY(g21,g17) = 50
    c: DistanceX(g16,g20) = 50
    c: DistanceX(g14,g10) = 50
    c: Equal(g22,g14)
    c: DistanceY(g8,g16) = 0
    c: DistanceY(g10,g18) = 0
    c: DistanceX(g4,g8) = 5
    c: DistanceY(g4,g8) = 5
    c: DistanceX(g6,g18) = -5
    c: DistanceY(g6,g18) = -5
    c: DistanceX(g9,g19) = 5
    c: PointOnObject(g13,g22)
    c: PointOnObject(g20,g12)
FEATURE [Part::FeaturePython] Window004  label="Fenêtre Chambre"  # WARN: FeaturePython — macro-defined, semantics opaque (R4)
  Base = -> Sketch005
  Height = 750
  HoleDepth = 0
  MoveWithHost = true
  Normal = (0,1,0)
  Preset = 3
  Role = 0
  Width = 1050
  WindowParts = <same value as first occurrence — deduplicated (x3 in doc)>
FEATURE [Sketcher::SketchObject] Sketch006
  Placement = pos=(8030,8165,0) rot=(0.57735,0.57735,0.57735;2.0944rad)
  sketch-geometry (8):
    g0: LineSegment StartX=0 StartY=0 StartZ=0 EndX=800 EndY=0 EndZ=0
    g1: LineSegment StartX=800 StartY=0 StartZ=0 EndX=800 EndY=2100 EndZ=0
    g2: LineSegment StartX=800 StartY=2100 StartZ=0 EndX=0 EndY=2100 EndZ=0
    g3: LineSegment StartX=0 StartY=2100 StartZ=0 EndX=0 EndY=0 EndZ=0
    g4: LineSegment StartX=50 StartY=0 StartZ=0 EndX=750 EndY=0 EndZ=0
    g5: LineSegment StartX=750 StartY=0 StartZ=0 EndX=750 EndY=2050 EndZ=0
    g6: LineSegment StartX=750 StartY=2050 StartZ=0 EndX=50 EndY=2050 EndZ=0
    g7: LineSegment StartX=50 StartY=2050 StartZ=0 EndX=50 EndY=0 EndZ=0
  constraints (23):
    c: Coincident(g0,g1)
    c: Coincident(g1,g2)
    c: Coincident(g2,g3)
    c: Coincident(g3,g0)
    c: Horizontal(g0)
    c: Horizontal(g2)
    c: Vertical(g1)
    c: Vertical(g3)
    c: Coincident(g4,g5)
    c: Coincident(g5,g6)
    c: Coincident(g6,g7)
    c: Coincident(g7,g4)
    c: Horizontal(g4)
    c: Horizontal(g6)
    c: Vertical(g5)
    c: Vertical(g7)
    c: DistanceY(g1) = 2100
    c: DistanceX(g0) = 800
    c: DistanceY(g6,g2) = 50
    c: DistanceX(g2,g6) = 50
    c: DistanceX(g4,g0) = 50
    c: DistanceY(g0,g4) = 0
    c: Coincident(g0,g-1)
FEATURE [Part::FeaturePython] Window005  label="Porte Intérieure"  # WARN: FeaturePython — macro-defined, semantics opaque (R4)
  Base = -> Sketch006
  Height = 2100
  HoleDepth = 0
  MoveWithHost = true
  Normal = (-1,0,0)
  Preset = 6
  Role = 1
  Width = 800
  WindowParts = OuterFrame | Frame | Wire0,Wire1 | 70.0 | 0.0 | Door | Solid panel | Wire1 | 50.0 | 10.0
FEATURE [Sketcher::SketchObject] Sketch007
  Placement = pos=(5230,8037.1,0) rot=(1,0,0;1.5708rad)
  sketch-geometry (8):
    g0: LineSegment StartX=0 StartY=0 StartZ=0 EndX=800 EndY=0 EndZ=0
    g1: LineSegment StartX=800 StartY=0 StartZ=0 EndX=800 EndY=2100 EndZ=0
    g2: LineSegment StartX=800 StartY=2100 StartZ=0 EndX=0 EndY=2100 EndZ=0
    g3: LineSegment StartX=0 StartY=2100 StartZ=0 EndX=0 EndY=0 EndZ=0
    g4: LineSegment StartX=50 StartY=0 StartZ=0 EndX=750 EndY=0 EndZ=0
    g5: LineSegment StartX=750 StartY=0 StartZ=0 EndX=750 EndY=2050 EndZ=0
    g6: LineSegment StartX=750 StartY=2050 StartZ=0 EndX=50 EndY=2050 EndZ=0
    g7: LineSegment StartX=50 StartY=2050 StartZ=0 EndX=50 EndY=0 EndZ=0
  constraints (23):
    c: Coincident(g0,g1)
    c: Coincident(g1,g2)
    c: Coincident(g2,g3)
    c: Coincident(g3,g0)
    c: Horizontal(g0)
    c: Horizontal(g2)
    c: Vertical(g1)
    c: Vertical(g3)
    c: Coincident(g4,g5)
    c: Coincident(g5,g6)
    c: Coincident(g6,g7)
    c: Coincident(g7,g4)
    c: Horizontal(g4)
    c: Horizontal(g6)
    c: Vertical(g5)
    c: Vertical(g7)
    c: DistanceY(g1) = 2100
    c: DistanceX(g0) = 800
    c: DistanceY(g6,g2) = 50
    c: DistanceX(g2,g6) = 50
    c: DistanceX(g4,g0) = 50
    c: DistanceY(g0,g4) = 0
    c: Coincident(g0,g-1)
FEATURE [Part::FeaturePython] Window006  label="Porte Intérieure001"  # WARN: FeaturePython — macro-defined, semantics opaque (R4)
  Base = -> Sketch007
  Height = 2100
  HoleDepth = 0
  MoveWithHost = true
  Normal = (0,0,0)
  Preset = 6
  Role = 1
  Width = 800
  WindowParts = OuterFrame | Frame | Wire0,Wire1 | 70.0 | 0.0 | Door | Solid panel | Wire1 | 50.0 | 10.0
FEATURE [Sketcher::SketchObject] Sketch008
  Placement = pos=(3090,8957.1,0) rot=(0.57735,-0.57735,-0.57735;2.0944rad)
  sketch-geometry (8):
    g0: LineSegment StartX=0 StartY=0 StartZ=0 EndX=800 EndY=0 EndZ=0
    g1: LineSegment StartX=800 StartY=0 StartZ=0 EndX=800 EndY=2100 EndZ=0
    g2: LineSegment StartX=800 StartY=2100 StartZ=0 EndX=0 EndY=2100 EndZ=0
    g3: LineSegment StartX=0 StartY=2100 StartZ=0 EndX=0 EndY=0 EndZ=0
    g4: LineSegment StartX=50 StartY=0 StartZ=0 EndX=750 EndY=0 EndZ=0
    g5: LineSegment StartX=750 StartY=0 StartZ=0 EndX=750 EndY=2050 EndZ=0
    g6: LineSegment StartX=750 StartY=2050 StartZ=0 EndX=50 EndY=2050 EndZ=0
    g7: LineSegment StartX=50 StartY=2050 StartZ=0 EndX=50 EndY=0 EndZ=0
  constraints (23):
    c: Coincident(g0,g1)
    c: Coincident(g1,g2)
    c: Coincident(g2,g3)
    c: Coincident(g3,g0)
    c: Horizontal(g0)
    c: Horizontal(g2)
    c: Vertical(g1)
    c: Vertical(g3)
    c: Coincident(g4,g5)
    c: Coincident(g5,g6)
    c: Coincident(g6,g7)
    c: Coincident(g7,g4)
    c: Horizontal(g4)
    c: Horizontal(g6)
    c: Vertical(g5)
    c: Vertical(g7)
    c: DistanceY(g1) = 2100
    c: DistanceX(g0) = 800
    c: DistanceY(g6,g2) = 50
    c: DistanceX(g2,g6) = 50
    c: DistanceX(g4,g0) = 50
    c: DistanceY(g0,g4) = 0
    c: Coincident(g0,g-1)
FEATURE [Part::FeaturePython] Window007  label="Porte Intérieure002"  # WARN: FeaturePython — macro-defined, semantics opaque (R4)
  Base = -> Sketch008
  Height = 2100
  HoleDepth = 100
  MoveWithHost = true
  Normal = (0,0,0)
  Preset = 6
  Role = 1
  Width = 800
  WindowParts = OuterFrame | Frame | Wire0,Wire1 | 70.0 | 0.0 | Door | Solid panel | Wire1 | 50.0 | 10.0
FEATURE [Sketcher::SketchObject] Sketch009
  Placement = pos=(250,7177.1,0) rot=(1,0,0;1.5708rad)
  sketch-geometry (8):
    g0: LineSegment StartX=0 StartY=0 StartZ=0 EndX=800 EndY=0 EndZ=0
    g1: LineSegment StartX=800 StartY=0 StartZ=0 EndX=800 EndY=2100 EndZ=0
    g2: LineSegment StartX=800 StartY=2100 StartZ=0 EndX=0 EndY=2100 EndZ=0
    g3: LineSegment StartX=0 StartY=2100 StartZ=0 EndX=0 EndY=0 EndZ=0
    g4: LineSegment StartX=50 StartY=0 StartZ=0 EndX=750 EndY=0 EndZ=0
    g5: LineSegment StartX=750 StartY=0 StartZ=0 EndX=750 EndY=2050 EndZ=0
    g6: LineSegment StartX=750 StartY=2050 StartZ=0 EndX=50 EndY=2050 EndZ=0
    g7: LineSegment StartX=50 StartY=2050 StartZ=0 EndX=50 EndY=0 EndZ=0
  constraints (23):
    c: Coincident(g0,g1)
    c: Coincident(g1,g2)
    c: Coincident(g2,g3)
    c: Coincident(g3,g0)
    c: Horizontal(g0)
    c: Horizontal(g2)
    c: Vertical(g1)
    c: Vertical(g3)
    c: Coincident(g4,g5)
    c: Coincident(g5,g6)
    c: Coincident(g6,g7)
    c: Coincident(g7,g4)
    c: Horizontal(g4)
    c: Horizontal(g6)
    c: Vertical(g5)
    c: Vertical(g7)
    c: DistanceY(g1) = 2100
    c: DistanceX(g0) = 800
    c: DistanceY(g6,g2) = 50
    c: DistanceX(g2,g6) = 50
    c: DistanceX(g4,g0) = 50
    c: DistanceY(g0,g4) = 0
    c: Coincident(g0,g-1)
FEATURE [Part::FeaturePython] Window008  label="Porte Intérieure003"  # WARN: FeaturePython — macro-defined, semantics opaque (R4)
  Base = -> Sketch009
  Height = 2100
  HoleDepth = 0
  MoveWithHost = true
  Normal = (0,0,0)
  Preset = 6
  Role = 1
  Width = 800
  WindowParts = OuterFrame | Frame | Wire0,Wire1 | 70.0 | 0.0 | Door | Solid panel | Wire1 | 50.0 | 10.0
FEATURE [Sketcher::SketchObject] Sketch010
  Placement = pos=(4020,7257.1,0) rot=(0.57735,-0.57735,-0.57735;2.0944rad)
  sketch-geometry (8):
    g0: LineSegment StartX=0 StartY=0 StartZ=0 EndX=700 EndY=0 EndZ=0
    g1: LineSegment StartX=700 StartY=0 StartZ=0 EndX=700 EndY=2100 EndZ=0
    g2: LineSegment StartX=700 StartY=2100 StartZ=0 EndX=0 EndY=2100 EndZ=0
    g3: LineSegment StartX=0 StartY=2100 StartZ=0 EndX=0 EndY=0 EndZ=0
    g4: LineSegment StartX=50 StartY=0 StartZ=0 EndX=650 EndY=0 EndZ=0
    g5: LineSegment StartX=650 StartY=0 StartZ=0 EndX=650 EndY=2050 EndZ=0
    g6: LineSegment StartX=650 StartY=2050 StartZ=0 EndX=50 EndY=2050 EndZ=0
    g7: LineSegment StartX=50 StartY=2050 StartZ=0 EndX=50 EndY=0 EndZ=0
  constraints (23):
    c: Coincident(g0,g1)
    c: Coincident(g1,g2)
    c: Coincident(g2,g3)
    c: Coincident(g3,g0)
    c: Horizontal(g0)
    c: Horizontal(g2)
    c: Vertical(g1)
    c: Vertical(g3)
    c: Coincident(g4,g5)
    c: Coincident(g5,g6)
    c: Coincident(g6,g7)
    c: Coincident(g7,g4)
    c: Horizontal(g4)
    c: Horizontal(g6)
    c: Vertical(g5)
    c: Vertical(g7)
    c: DistanceY(g1) = 2100
    c: DistanceX(g0) = 700
    c: DistanceY(g6,g2) = 50
    c: DistanceX(g2,g6) = 50
    c: DistanceX(g4,g0) = 50
    c: DistanceY(g0,g4) = 0
    c: Coincident(g0,g-1)
FEATURE [Part::FeaturePython] Window009  label="Porte Intérieure004"  # WARN: FeaturePython — macro-defined, semantics opaque (R4)
  Base = -> Sketch010
  Height = 2100
  HoleDepth = 100
  MoveWithHost = true
  Normal = (0,0,0)
  Preset = 6
  Role = 1
  Width = 800
  WindowParts = OuterFrame | Frame | Wire0,Wire1 | 70.0 | 0.0 | Door | Solid panel | Wire1 | 50.0 | 10.0
FEATURE [Part::Box] Box  label="Cube"
  Height = 400
  Length = 900
  Placement = pos=(4020,1150,200) rot=(0,0,1;1.5708rad)
  Width = 100
FEATURE [Sketcher::SketchObject] Sketch011
  Placement = pos=(2075,166.296,0) rot=(0.57735,0.57735,0.57735;2.0944rad)
  sketch-geometry (6):
    g0: LineSegment StartX=433.704 StartY=800 StartZ=0 EndX=433.704 EndY=2677.66 EndZ=0
    g1: LineSegment StartX=300 StartY=3671.64 StartZ=0 EndX=300 EndY=3000.45 EndZ=0
    g2: ArcOfCircle CenterX=528.247 CenterY=3000.45 CenterZ=0 NormalX=0 NormalY=0 NormalZ=1 Radius=228.247 StartAngle=3.14159 EndAngle=3.92699
    g3: ArcOfCircle CenterX=205.457 CenterY=2677.66 CenterZ=0 NormalX=0 NormalY=0 NormalZ=1 Radius=228.247 StartAngle=0 EndAngle=0.785398
    g4: LineSegment [constr] StartX=366.852 StartY=2839.05 StartZ=0 EndX=433.704 EndY=2772.2 EndZ=0
    g5: LineSegment [constr] StartX=433.704 StartY=2772.2 StartZ=0 EndX=433.704 EndY=2677.66 EndZ=0
  constraints (16):
    c: Vertical(g0)
    c: Vertical(g1)
    c: Coincident(g2,g1)
    c: Coincident(g3,g2)
    c: Tangent(g2,g1)
    c: Tangent(g2,g3)
    c: Equal(g2,g3)
    c: Tangent(g0,g3) = -1.5708
    c: DistanceX(g1) = 300
    c: Coincident(g4,g5)
    c: Coincident(g5,g0)
    c: Vertical(g5)
    c: Tangent(g2,g4)
    c: Coincident(g4,g2)
    c: DistanceY(g0) = 800
    c: Angle(g4) = -0.785398
FEATURE [Sketcher::SketchObject] Sketch012
  Placement = pos=(1700,400,800) rot=(0,0,1;0rad)
  sketch-geometry (1):
    g0: Circle CenterX=375 CenterY=200 CenterZ=0 NormalX=0 NormalY=0 NormalZ=1 Radius=75
  constraints (1):
    c: Radius(g0) = 75
FEATURE [Part::Sweep] Sweep
  Frenet = false
  Sections = -> [Sketch012]
  Solid = true
  Spine = -> Sketch011
  Transition = 1
FEATURE [Part::Box] Box001  label="Cube001"
  Height = 1500
  Length = 100
  Placement = pos=(200,4440,100) rot=(0,0,1;0rad)
  Width = 400
FEATURE [Part::Feature] MultiTransform001  label="Poele à bois001"
  Placement = pos=(1700,400,220) rot=(0,0,1;0rad)
  shape: bbox 750 x 400 x 800 mm, 26 faces (baked)
FEATURE [Part::FeaturePython] Equipment  label="Radiateur"  # WARN: FeaturePython — macro-defined, semantics opaque (R4)
  Base = -> Box001
  MoveWithHost = false
  Role = 2
FEATURE [Part::FeaturePython] Equipment001  label="Poele à bois"  # WARN: FeaturePython — macro-defined, semantics opaque (R4)
  Base = -> MultiTransform001
  MoveWithHost = false
  Role = 0
FEATURE [Part::Feature] Compound001
  Placement = pos=(220,2500,0) rot=(0,0,1;0rad)
  shape: bbox 950 x 1720 x 830 mm, 48 faces, 8 solids (baked)
FEATURE [Part::FeaturePython] Equipment002  label="XENA"  # WARN: FeaturePython — macro-defined, semantics opaque (R4)
  Base = -> Compound001
  Description = CANAPE 3PL RAPIDO 140
  MoveWithHost = false
  Role = 0
FEATURE [Part::Feature] Fillet001
  Placement = pos=(4020,500,290) rot=(0.57735,-0.57735,-0.57735;2.0944rad)
  shape: bbox 10 x 113.1 x 113.1 mm, 14 faces (baked)
FEATURE [Part::FeaturePython] Equipment003  label="PriseElecMurale"  # WARN: FeaturePython — macro-defined, semantics opaque (R4)
  Base = -> Fillet001
  MoveWithHost = false
  Role = 2
FEATURE [Part::FeaturePython] Equipment004  label="PriseElecMurale001"  # WARN: FeaturePython — macro-defined, semantics opaque (R4)
  CloneOf = -> Equipment003
  MoveWithHost = false
  Placement = pos=(0,-100,0) rot=(0,0,1;0rad)
  Role = 0
FEATURE [Part::FeaturePython] Equipment005  label="PriseElecMurale002"  # WARN: FeaturePython — macro-defined, semantics opaque (R4)
  CloneOf = -> Equipment003
  MoveWithHost = false
  Placement = pos=(0,-200,0) rot=(0,0,1;0rad)
  Role = 0
FEATURE [Part::FeaturePython] Equipment006  label="Radiateur001"  # WARN: FeaturePython — macro-defined, semantics opaque (R4)
  Base = -> Box
  MoveWithHost = false
  Role = 0
FEATURE [Part::Part2DObjectPython] Rectangle  label="Convertible Déplié"  # Draft 2D object (typed FeaturePython)
  ChamferSize = 0
  FilletRadius = 0
  Height = 1720
  Length = 2120
  MakeFace = false
  Placement = pos=(220,2500,50) rot=(0,0,1;0rad)
FEATURE [Part::Feature] Compound002
  Placement = pos=(-500,0,0) rot=(0,0,1;1.5708rad)
  shape: bbox 750 x 1500 x 744 mm, 18 faces, 5 solids (baked)
FEATURE [Part::FeaturePython] Equipment007  label="Bureau Jo"  # WARN: FeaturePython — macro-defined, semantics opaque (R4)
  Base = -> Compound002
  MoveWithHost = false
  Placement = pos=(4520,2568.04,0) rot=(0,0,1;0rad)
  Role = 0
FEATURE [Part::Box] Box003  label="Cube003"
  Height = 810
  Length = 1780
  Placement = pos=(4020,560,0) rot=(0,0,1;1.5708rad)
  Width = 420
FEATURE [Part::FeaturePython] Equipment008  label="Buffet"  # WARN: FeaturePython — macro-defined, semantics opaque (R4)
  Base = -> Box003
  MoveWithHost = false
  Role = 0
FEATURE [Part::Feature] MultiTransform002
  Placement = pos=(615,1000,0) rot=(0,0,1;1.5708rad)
  shape: bbox 400 x 1250 x 1800 mm, 66 faces (baked)
FEATURE [Part::FeaturePython] Equipment009  label="Étagère"  # WARN: FeaturePython — macro-defined, semantics opaque (R4)
  Base = -> MultiTransform002
  MoveWithHost = false
  Role = 0
FEATURE [Part::Feature] Compound003
  Placement = pos=(2936.54,3385.75,0) rot=(0,0,1;3.14159rad)
  shape: bbox 611.7 x 643.1 x 1270 mm, 53 faces, 9 solids (baked)
FEATURE [Part::FeaturePython] Equipment010  label="Chaise de bureau"  # WARN: FeaturePython — macro-defined, semantics opaque (R4)
  Base = -> Compound003
  MoveWithHost = false
  Role = 0
FEATURE [Part::Feature] Compound004
  Placement = pos=(3000,1400,0) rot=(0,0,1;0.785398rad)
  shape: bbox 790.5 x 790.5 x 955.2 mm, 70 faces, 2 solids (baked)
FEATURE [Part::FeaturePython] Equipment012  label="Fauteil Ikea"  # WARN: FeaturePython — macro-defined, semantics opaque (R4)
  Base = -> Compound004
  MoveWithHost = false
  Role = 0
FEATURE [Part::Feature] Compound005
  Placement = pos=(1500,2000,0) rot=(0,0,1;2.49582rad)
  shape: bbox 787.3 x 782.7 x 955.2 mm, 70 faces, 2 solids (baked)
FEATURE [Part::FeaturePython] Equipment013  label="Fauteil Ikea001"  # WARN: FeaturePython — macro-defined, semantics opaque (R4)
  Base = -> Compound005
  MoveWithHost = false
  Role = 0
FEATURE [Part::Cylinder] Cylinder  label="Cylindre"
  Angle = 360
  Height = 900
  Placement = pos=(500,8500,1550) rot=(0,0,1;0rad)
  Radius = 250
FEATURE [Part::FeaturePython] Equipment014  label="Ballon Eau Chaude"  # WARN: FeaturePython — macro-defined, semantics opaque (R4)
  Base = -> Cylinder
  MoveWithHost = false
  Role = 1
FEATURE [Part::Feature] Fusion001
  Placement = pos=(3800,387,0) rot=(0,0,1;0rad)
  shape: bbox 292.2 x 292.2 x 1846 mm, 10 faces (baked)
FEATURE [Part::FeaturePython] Equipment015  label="Halogen"  # WARN: FeaturePython — macro-defined, semantics opaque (R4)
  Base = -> Fusion001
  MoveWithHost = false
  Role = 2
FEATURE [Part::Feature] Compound006
  Placement = pos=(2355.92,4936.3,0) rot=(0,0,1;1.0122rad)
  shape: bbox 695.4 x 848 x 740 mm, 34 faces, 3 solids (baked)
FEATURE [Part::FeaturePython] Equipment016  label="TableNorden"  # WARN: FeaturePython — macro-defined, semantics opaque (R4)
  Base = -> Compound006
  MoveWithHost = false
  Role = 0
FEATURE [Part::FeaturePython] Equipment017  label="PriseElecMurale003"  # WARN: FeaturePython — macro-defined, semantics opaque (R4)
  CloneOf = -> Equipment003
  MoveWithHost = false
  Placement = pos=(0,3617,0) rot=(0,0,1;0rad)
  Role = 0
FEATURE [Part::FeaturePython] Equipment018  label="PriseElecMurale004"  # WARN: FeaturePython — macro-defined, semantics opaque (R4)
  CloneOf = -> Equipment003
  MoveWithHost = false
  Placement = pos=(4220,3970,0) rot=(0,0,1;3.14159rad)
  Role = 0
FEATURE [Part::FeaturePython] Equipment019  label="PriseElecMurale005"  # WARN: FeaturePython — macro-defined, semantics opaque (R4)
  CloneOf = -> Equipment003
  MoveWithHost = false
  Placement = pos=(4220,1640,0) rot=(0,0,1;3.14159rad)
  Role = 0
FEATURE [Part::FeaturePython] Structure  # WARN: FeaturePython — macro-defined, semantics opaque (R4)
  Height = 220
  Length = 4020
  MoveWithHost = false
  Nodes = (2) [(0,0,0),(4020,0,0)]
  Normal = (0,0,0)
  Placement = pos=(100,3357,2650) rot=(0,0,1;0rad)
  Role = 0
  Width = 90
FEATURE [Part::FeaturePython] TimberBeam  # WARN: FeaturePython — macro-defined, semantics opaque (R4)
  Base = -> Structure
  Height = 220
  Length = 4020
  Moise = false
  MoveWithHost = false
  Normal = (0,0,0)
  Placement = pos=(100,3357,2650) rot=(0,0,1;0rad)
  Preset = 0
  Role = 0
  Width = 90
FEATURE [Part::Feature] Compound007
  Placement = pos=(4020,3190,2540) rot=(0,0,1;1.5708rad)
  shape: bbox 85 x 2250 x 1305 mm, 16 faces, 3 solids (baked)
FEATURE [Part::FeaturePython] Equipment020  label="Ecran projection"  # WARN: FeaturePython — macro-defined, semantics opaque (R4)
  Base = -> Compound007
  MoveWithHost = false
  Role = 0
FEATURE [Part::Box] Box004  label="Cube004"
  Height = 114
  Length = 315
  Placement = pos=(1324,3199.5,2426) rot=(0,0,1;1.5708rad)
  Width = 224
FEATURE [Part::FeaturePython] Equipment021  label="Vidéo projecteur"  # WARN: FeaturePython — macro-defined, semantics opaque (R4)
  Base = -> Box004
  MoveWithHost = false
  Role = 0
FEATURE [Part::Part2DObjectPython] Line004  # Draft 2D object (typed FeaturePython)
  ChamferSize = 0
  Closed = false
  End = (10950,9277.1,0)
  FilletRadius = 0
  Length = 3670
  MakeFace = false
  Points = (2) [(10950,5607.1,0),(10950,9277.1,0)]
  Start = (10950,5607.1,0)
FEATURE [Part::Part2DObjectPython] Line005  # Draft 2D object (typed FeaturePython)
  ChamferSize = 0
  Closed = false
  End = (10950,9277.1,1982)
  FilletRadius = 0
  Length = 3670
  MakeFace = false
  Points = (2) [(10950,5607.1,1982),(10950,9277.1,1982)]
  Start = (10950,5607.1,1982)
FEATURE [Part::Part2DObjectPython] Line006  # Draft 2D object (typed FeaturePython)
  ChamferSize = 0
  Closed = false
  End = (10950,9277.1,2427)
  FilletRadius = 0
  Length = 3670
  MakeFace = false
  Points = (2) [(10950,5607.1,2427),(10950,9277.1,2427)]
  Start = (10950,5607.1,2427)
FEATURE [Part::Part2DObjectPython] Line007  # Draft 2D object (typed FeaturePython)
  ChamferSize = 0
  Closed = false
  End = (10950,5877.1,1982)
  FilletRadius = 0
  Length = 3195.73
  MakeFace = false
  Points = (2) [(10950,9007.1,2626.84),(10950,5877.1,1982)]
  Start = (10950,9007.1,2626.84)
FEATURE [Part::Part2DObjectPython] Line008  # Draft 2D object (typed FeaturePython)
  ChamferSize = 0
  Closed = false
  End = (10950,9121.18,3712.92)
  FilletRadius = 0
  Length = 3696.88
  MakeFace = false
  Points = (2) [(10950,5451.18,3267.92),(10950,9121.18,3712.92)]
  Start = (10950,5451.18,3267.92)
FEATURE [Part::Feature] Compound008
  Placement = pos=(7816,6434.39,0) rot=(0,0,1;3.14159rad)
  shape: bbox 1064 x 500 x 1540 mm, 51 faces, 11 solids (baked)
FEATURE [Part::FeaturePython] Equipment022  label="Vélo Elliptique"  # WARN: FeaturePython — macro-defined, semantics opaque (R4)
  Base = -> Compound008
  MoveWithHost = false
  Role = 0
FEATURE [Part::Feature] MultiTransform003
  Placement = pos=(5910,5877.1,738) rot=(0,0,1;1.5708rad)
  shape: bbox 700 x 1100 x 760 mm, 26 faces (baked)
FEATURE [Part::FeaturePython] Equipment023  label="Bureau Morgane"  # WARN: FeaturePython — macro-defined, semantics opaque (R4)
  Base = -> MultiTransform003
  MoveWithHost = false
  Role = 0
FEATURE [Part::Feature] Draft001
  Placement = pos=(6560,7237.1,0) rot=(0,0,1;0rad)
  shape: bbox 1400 x 800 x 1200 mm, 6 faces (baked)
FEATURE [Part::FeaturePython] Equipment024  label="Batterie"  # WARN: FeaturePython — macro-defined, semantics opaque (R4)
  Base = -> Draft001
  MoveWithHost = false
  Role = 0
FEATURE [Part::Box] Box005  label="Cube005"
  Height = 1980
  Length = 600
  Placement = pos=(10080,5967,0) rot=(0,0,1;0rad)
  Width = 500
FEATURE [Part::Box] Box006  label="Cube006"
  Height = 1980
  Length = 600
  Placement = pos=(10080,8167,0) rot=(0,0,1;0rad)
  Width = 500
FEATURE [Part::Box] Box007  label="Cube007"
  Height = 500
  Length = 2000
  Placement = pos=(8680,6617,0) rot=(0,0,1;0rad)
  Width = 1400
FEATURE [Part::FeaturePython] Equipment025  label="Lit"  # WARN: FeaturePython — macro-defined, semantics opaque (R4)
  Base = -> Box007
  MoveWithHost = false
  Role = 0
FEATURE [Part::FeaturePython] Equipment026  label="Placard001"  # WARN: FeaturePython — macro-defined, semantics opaque (R4)
  Base = -> Box006
  MoveWithHost = false
  Role = 0
FEATURE [Part::FeaturePython] Equipment027  label="Placard002"  # WARN: FeaturePython — macro-defined, semantics opaque (R4)
  Base = -> Box005
  MoveWithHost = false
  Role = 0
FEATURE [Sketcher::SketchObject] Sketch013
  Placement = pos=(5180,8037.1,0) rot=(0.57735,-0.57735,-0.57735;2.0944rad)
  sketch-geometry (8):
    g0: LineSegment StartX=0 StartY=0 StartZ=0 EndX=710 EndY=0 EndZ=0
    g1: LineSegment StartX=710 StartY=0 StartZ=0 EndX=710 EndY=2100 EndZ=0
    g2: LineSegment StartX=710 StartY=2100 StartZ=0 EndX=0 EndY=2100 EndZ=0
    g3: LineSegment StartX=0 StartY=2100 StartZ=0 EndX=0 EndY=0 EndZ=0
    g4: LineSegment StartX=10 StartY=0 StartZ=0 EndX=700 EndY=0 EndZ=0
    g5: LineSegment StartX=700 StartY=0 StartZ=0 EndX=700 EndY=2090 EndZ=0
    g6: LineSegment StartX=700 StartY=2090 StartZ=0 EndX=10 EndY=2090 EndZ=0
    g7: LineSegment StartX=10 StartY=2090 StartZ=0 EndX=10 EndY=0 EndZ=0
  constraints (23):
    c: Coincident(g0,g1)
    c: Coincident(g1,g2)
    c: Coincident(g2,g3)
    c: Coincident(g3,g0)
    c: Horizontal(g0)
    c: Horizontal(g2)
    c: Vertical(g1)
    c: Vertical(g3)
    c: Coincident(g4,g5)
    c: Coincident(g5,g6)
    c: Coincident(g6,g7)
    c: Coincident(g7,g4)
    c: Horizontal(g4)
    c: Horizontal(g6)
    c: Vertical(g5)
    c: Vertical(g7)
    c: DistanceY(g1) = 2100
    c: DistanceX(g0) = 710
    c: DistanceY(g6,g2) = 10
    c: DistanceX(g2,g6) = 10
    c: DistanceX(g4,g0) = 10
    c: DistanceY(g0,g4) = 0
    c: Coincident(g0,g-1)
FEATURE [Part::FeaturePython] Window010  label="Porte Placard"  # WARN: FeaturePython — macro-defined, semantics opaque (R4)
  Base = -> Sketch013
  Height = 2100
  HoleDepth = 70
  MoveWithHost = true
  Normal = (1,0,0)
  Preset = 6
  Role = 1
  Width = 710
  WindowParts = OuterFrame | Frame | Wire0,Wire1 | 10.0 | 10.0 | Door | Solid panel | Wire1 | 10.0 | 20.0
FEATURE [Sketcher::SketchObject] Sketch014
  Placement = pos=(4020,8037.1,0) rot=(0.57735,-0.57735,-0.57735;2.0944rad)
  sketch-geometry (8):
    g0: LineSegment StartX=0 StartY=0 StartZ=0 EndX=710 EndY=0 EndZ=0
    g1: LineSegment StartX=710 StartY=0 StartZ=0 EndX=710 EndY=2100 EndZ=0
    g2: LineSegment StartX=710 StartY=2100 StartZ=0 EndX=0 EndY=2100 EndZ=0
    g3: LineSegment StartX=0 StartY=2100 StartZ=0 EndX=0 EndY=0 EndZ=0
    g4: LineSegment StartX=10 StartY=0 StartZ=0 EndX=700 EndY=0 EndZ=0
    g5: LineSegment StartX=700 StartY=0 StartZ=0 EndX=700 EndY=2090 EndZ=0
    g6: LineSegment StartX=700 StartY=2090 StartZ=0 EndX=10 EndY=2090 EndZ=0
    g7: LineSegment StartX=10 StartY=2090 StartZ=0 EndX=10 EndY=0 EndZ=0
  constraints (23):
    c: Coincident(g0,g1)
    c: Coincident(g1,g2)
    c: Coincident(g2,g3)
    c: Coincident(g3,g0)
    c: Horizontal(g0)
    c: Horizontal(g2)
    c: Vertical(g1)
    c: Vertical(g3)
    c: Coincident(g4,g5)
    c: Coincident(g5,g6)
    c: Coincident(g6,g7)
    c: Coincident(g7,g4)
    c: Horizontal(g4)
    c: Horizontal(g6)
    c: Vertical(g5)
    c: Vertical(g7)
    c: DistanceY(g1) = 2100
    c: DistanceX(g0) = 710
    c: DistanceY(g6,g2) = 10
    c: DistanceX(g2,g6) = 10
    c: DistanceX(g4,g0) = 10
    c: DistanceY(g0,g4) = 0
    c: Coincident(g0,g-1)
FEATURE [Part::FeaturePython] Window011  label="Porte Placard001"  # WARN: FeaturePython — macro-defined, semantics opaque (R4)
  Base = -> Sketch014
  Height = 2100
  HoleDepth = 70
  MoveWithHost = true
  Normal = (1,0,0)
  Preset = 6
  Role = 1
  Width = 710
  WindowParts = OuterFrame | Frame | Wire0,Wire1 | 10.0 | 10.0 | Door | Solid panel | Wire1 | 10.0 | 20.0
FEATURE [Part::Part2DObjectPython] Line009  # Draft 2D object (typed FeaturePython)
  ChamferSize = 0
  Closed = false
  End = (10950,5877.1,3000)
  FilletRadius = 0
  Length = 3000
  MakeFace = false
  Placement = pos=(0,270,0) rot=(0,0,1;0rad)
  Points = (2) [(10950,5607.1,0),(10950,5607.1,3000)]
  Start = (10950,5877.1,0)
FEATURE [Part::Part2DObjectPython] Line010  # Draft 2D object (typed FeaturePython)
  ChamferSize = 0
  Closed = false
  End = (10950,9007.1,3000)
  FilletRadius = 0
  Length = 3000
  MakeFace = false
  Points = (2) [(10950,9007.1,0),(10950,9007.1,3000)]
  Start = (10950,9007.1,0)
FEATURE [Part::Feature] Compound009
  Placement = pos=(500,500,0) rot=(0,0,1;0rad)
  shape: bbox 530 x 530 x 1370 mm, 22 faces, 4 solids (baked)
FEATURE [Part::FeaturePython] Equipment028  label="Batterie Empilée"  # WARN: FeaturePython — macro-defined, semantics opaque (R4)
  Base = -> Compound009
  MoveWithHost = false
  Role = 0
FEATURE [Part::Box] Box008  label="Cube008"
  Height = 600
  Length = 100
  Placement = pos=(7640,5877.1,160) rot=(0,0,1;1.5708rad)
  Width = 450
FEATURE [Part::FeaturePython] Equipment029  label="Radiateur002"  # WARN: FeaturePython — macro-defined, semantics opaque (R4)
  Base = -> Box008
  MoveWithHost = false
  Role = 2
FEATURE [Part::Part2DObjectPython] Rectangle001  # Draft 2D object (typed FeaturePython)
  ChamferSize = 0
  FilletRadius = 0
  Height = 900
  Length = -4800
  MakeFace = false
  Placement = pos=(7960,8107.1,2350) rot=(0,0,1;0rad)
FEATURE [Part::FeaturePython] Structure001  # WARN: FeaturePython — macro-defined, semantics opaque (R4)
  Base = -> Rectangle001
  Height = 50
  Length = 0
  MoveWithHost = false
  Normal = (0,0,0)
  Role = 0
  Width = 100
FEATURE [Part::Part2DObjectPython] Line011  # Draft 2D object (typed FeaturePython)
  ChamferSize = 0
  Closed = false
  End = (10950,9007.1,2477.5)
  FilletRadius = 0
  Length = 3161.48
  MakeFace = false
  Points = (2) [(10950,5877.1,2032.5),(10950,9007.1,2477.5)]
  Start = (10950,5877.1,2032.5)
FEATURE [Part::Part2DObjectPython] DWire003  # Draft 2D object (typed FeaturePython)
  ChamferSize = 0
  Closed = true
  End = (10680,5877.1,2032.5)
  FilletRadius = 0
  Length = 6493.13
  MakeFace = false
  Placement = pos=(-270,0,0) rot=(0,0,1;0rad)
  Points = (4) [(10950,5877.1,1982),(10950,9007.1,2626.84),(10950,9007.1,2677.89),(10950,5877.1,2032.5)]
  Start = (10680,5877.1,1982)
FEATURE [Part::Extrusion] Extrude_DWire003  label="DWire003_Extrude"
  Base = -> DWire003
  Dir = (-10480,0,0)
  Solid = true
FEATURE [Part::Part2DObjectPython] Line012  # Draft 2D object (typed FeaturePython)
  ChamferSize = 0
  Closed = false
  End = (10950,8037.1,3000)
  FilletRadius = 0
  Length = 2990
  MakeFace = false
  Points = (2) [(7960,8037.1,3000),(10950,8037.1,3000)]
  Start = (7960,8037.1,3000)
FEATURE [Part::Part2DObjectPython] Line013  # Draft 2D object (typed FeaturePython)
  ChamferSize = 0
  Closed = false
  End = (10950,9007.1,3000)
  FilletRadius = 0
  Length = 0
  MakeFace = false
  Start = (0,0,0)
FEATURE [Part::Part2DObjectPython] Line014  # Draft 2D object (typed FeaturePython)
  ChamferSize = 0
  Closed = false
  End = (10950,8037.1,3000)
  FilletRadius = 0
  Length = 3000
  MakeFace = false
  Points = (2) [(10950,8037.1,0),(10950,8037.1,3000)]
  Start = (10950,8037.1,0)
FEATURE [Part::Part2DObjectPython] Line015  # Draft 2D object (typed FeaturePython)
  ChamferSize = 0
  Closed = false
  End = (10950,9277.1,2733.51)
  FilletRadius = 0
  Length = 3798.12
  MakeFace = false
  Points = (2) [(10950,5557.1,1967.12),(10950,9277.1,2733.51)]
  Start = (10950,5557.1,1967.12)
FEATURE [Part::Part2DObjectPython] Line016  # Draft 2D object (typed FeaturePython)
  ChamferSize = 0
  Closed = false
  End = (10950,8037.1,2478.05)
  FilletRadius = 0
  Length = 2205.36
  MakeFace = false
  Points = (2) [(10950,5877.1,2033.05),(10950,8037.1,2478.05)]
  Start = (10950,5877.1,2033.05)
FEATURE [Part::Part2DObjectPython] Line017  # Draft 2D object (typed FeaturePython)
  ChamferSize = 0
  Closed = false
  End = (10950,8037.1,2427)
  FilletRadius = 0
  Length = 2205.36
  MakeFace = false
  Points = (2) [(10950,5877.1,1982),(10950,8037.1,2427)]
  Start = (10950,5877.1,1982)
FEATURE [Mesh::Feature] Polantis_wc_03_3d  label="Polantis-wc_03-3d"
  Placement = pos=(4881,6552,0) rot=(0,0.707107,0.707107;3.14159rad)
FEATURE [Mesh::FeaturePython] Equipment030  label="WC"  # WARN: FeaturePython — macro-defined, semantics opaque (R4)
  Base = -> Polantis_wc_03_3d
  MoveWithHost = false
  Placement = pos=(4881,6552,0) rot=(0,0.707107,0.707107;3.14159rad)
  Role = 0
FEATURE [Part::Part2DObjectPython] DWire005  # Draft 2D object (typed FeaturePython)
  ChamferSize = 0
  Closed = false
  End = (8610.07,8520.92,500)
  FilletRadius = 0
  Length = 42722.6
  MakeFace = false
  Placement = pos=(0,0,-1000) rot=(0,0,1;0rad)
  Points = (25) [(14971.8,-863.222,1500),(8367.82,4529.73,1500),(4815.57,4949.54,1500),(3556.14,4917.25,1500),(2571.2,4449,1500),(1430.96,2276.03,1500),+19 more]
  Start = (14971.8,-863.222,500)
FEATURE [App::DocumentObjectGroup] Groupe  label="Visite"
  Group = -> [DWire005]
FEATURE [Part::Part2DObjectPython] DWire006  # Draft 2D object (typed FeaturePython)
  ChamferSize = 0
  Closed = true
  End = (2055.44,5229.12,1160)
  FilletRadius = 0
  Length = 2000
  MakeFace = true
  Points = (4) [(2479.44,5907.52,1160),(2649.04,5801.52,1160),(2225.04,5123.12,1160),(2055.44,5229.12,1160)]
  Start = (2479.44,5907.52,1160)
FEATURE [Part::Part2DObjectPython] Line018  # Draft 2D object (typed FeaturePython)
  ChamferSize = 0
  Closed = false
  End = (2055.44,5229.12,1160)
  FilletRadius = 0
  Length = 200
  MakeFace = false
  Points = (2) [(2225.04,5123.12,1160),(2055.44,5229.12,1160)]
  Start = (2225.04,5123.12,1160)
FEATURE [Part::Extrusion] Extrusion
  Base = -> DWire006
  Dir = (0,0,-200)
  Solid = true
FEATURE [Part::FeaturePython] Wall011  label="Cloison Bar"  # WARN: FeaturePython — macro-defined, semantics opaque (R4)
  Align = 1
  Base = -> DWire001
  Face = 0
  Height = 1160
  Length = 0
  MoveWithHost = false
  Normal = (0,0,0)
  Role = 0
  Subtractions = -> [Extrusion]
  Width = 70
FEATURE [Part::Part2DObjectPython] Line019  # Draft 2D object (typed FeaturePython)
  ChamferSize = 0
  Closed = false
  End = (2028.8,5186.5,1160)
  FilletRadius = 0
  Length = 850.261
  MakeFace = false
  Points = (2) [(2479.44,5907.52,1160),(2028.8,5186.5,1160)]
  Start = (2479.44,5907.52,1160)
FEATURE [Part::Part2DObjectPython] Line020  # Draft 2D object (typed FeaturePython)
  ChamferSize = 0
  Closed = false
  End = (2198.4,5080.5,1160)
  FilletRadius = 0
  Length = 850.261
  MakeFace = false
  Points = (2) [(2649.04,5801.52,1160),(2198.4,5080.5,1160)]
  Start = (2649.04,5801.52,1160)
FEATURE [Part::Part2DObjectPython] Line021  # Draft 2D object (typed FeaturePython)
  ChamferSize = 0
  Closed = false
  End = (2479.44,5907.52,1160)
  FilletRadius = 0
  Length = 200
  MakeFace = false
  Points = (2) [(2649.04,5801.52,1160),(2479.44,5907.52,1160)]
  Start = (2649.04,5801.52,1160)
FEATURE [Sketcher::SketchObject] Sketch015
  Placement = pos=(0,0,960) rot=(0,0,1;0rad)
  sketch-geometry (11):
    g0: ArcOfCircle CenterX=2113.74 CenterY=5228.06 CenterZ=0 NormalX=0 NormalY=0 NormalZ=1 Radius=59.9999 StartAngle=2.58299 EndAngle=4.15379
    g1: ArcOfCircle CenterX=2173.1 CenterY=5190.96 CenterZ=0 NormalX=0 NormalY=0 NormalZ=1 Radius=60.0001 StartAngle=4.15379 EndAngle=5.72458
    g2: LineSegment StartX=2141.3 StartY=5140.08 StartZ=0 EndX=2157.2 EndY=5165.52 EndZ=0
    g3: LineSegment StartX=2157.2 StartY=5165.52 StartZ=0 EndX=2097.84 EndY=5202.62 EndZ=0
    g4: LineSegment StartX=2097.84 StartY=5202.62 StartZ=0 EndX=2081.94 EndY=5177.18 EndZ=0
    g5: LineSegment StartX=2062.86 StartY=5259.86 StartZ=0 EndX=2441.81 EndY=5866.18 EndZ=0
    g6: LineSegment StartX=2602.93 StartY=5765.48 StartZ=0 EndX=2223.98 EndY=5159.16 EndZ=0
    g7: LineSegment StartX=2503.82 StartY=5880.49 StartZ=0 EndX=2588.62 EndY=5827.49 EndZ=0
    g8: ArcOfCircle CenterX=2564.77 CenterY=5789.33 CenterZ=0 NormalX=0 NormalY=0 NormalZ=1 Radius=45 StartAngle=5.72459 EndAngle=7.29538
    g9: ArcOfCircle CenterX=2479.97 CenterY=5842.33 CenterZ=0 NormalX=0 NormalY=0 NormalZ=1 Radius=45 StartAngle=1.0122 EndAngle=2.58299
    g10: LineSegment [constr] StartX=2081.94 StartY=5177.18 StartZ=0 EndX=2141.3 EndY=5140.08 EndZ=0
  constraints (12):
    c: Coincident(g0,g4)
    c: Coincident(g0,g5)
    c: Coincident(g0,g10)
    c: Coincident(g6,g1)
    c: Coincident(g10,g1)
    c: Coincident(g3,g2)
    c: Coincident(g10,g2)
    c: Coincident(g4,g3)
    c: Coincident(g5,g9)
    c: Coincident(g6,g8)
    c: Coincident(g7,g8)
    c: Coincident(g7,g9)
FEATURE [Part::FeaturePython] Structure002  # WARN: FeaturePython — macro-defined, semantics opaque (R4)
  Base = -> Sketch015
  Height = 28
  Length = 0
  MoveWithHost = false
  Normal = (0,0,0)
  Role = 0
  Width = 100
FEATURE [Part::Feature] Face
  shape: bbox 2014 x 446 x 2e-07 mm, 1 faces, 0 solids (baked)
FEATURE [Part::Extrusion] Extrusion001
  Base = -> Face
  Dir = (0,0,-40)
  Solid = true
FEATURE [Part::Part2DObjectPython] Rectangle002  # Draft 2D object (typed FeaturePython)
  ChamferSize = 0
  FilletRadius = 0
  Height = 710
  Length = -490
  MakeFace = false
  Placement = pos=(5140,7327.1,3000) rot=(0,0,1;0rad)
FEATURE [Part::Part2DObjectPython] Rectangle003  # Draft 2D object (typed FeaturePython)
  ChamferSize = 0
  FilletRadius = 0
  Height = 710
  Length = -490
  MakeFace = false
  Placement = pos=(4580,7327.1,3000) rot=(0,0,1;0rad)
FEATURE [Part::Part2DObjectPython] DWire007  # Draft 2D object (typed FeaturePython)
  ChamferSize = 0
  Closed = true
  End = (4290,5877.1,3000)
  FilletRadius = 0
  Length = 4860
  MakeFace = false
  Points = (6) [(5140,5877.1,3000),(5140,7257.1,3000),(4090,7257.1,3000),(4090,6557.1,3000),(4290,6557.1,3000),(4290,5877.1,3000)]
  Start = (5140,5877.1,3000)
FEATURE [Part::Part2DObjectPython] Rectangle004  # Draft 2D object (typed FeaturePython)
  ChamferSize = 0
  FilletRadius = 0
  Height = 2160
  Length = -2750
  MakeFace = false
  Placement = pos=(7960,5877.1,3000) rot=(0,0,1;0rad)
FEATURE [Part::Part2DObjectPython] Rectangle005  # Draft 2D object (typed FeaturePython)
  ChamferSize = 0
  FilletRadius = 0
  Height = 3130
  Length = -2650
  MakeFace = false
  Placement = pos=(10680,5877.1,3000) rot=(0,0,1;0rad)
FEATURE [Part::Extrusion] Extrude_Rectangle002  label="Rectangle002_Extrude"
  Base = -> Rectangle002
  Dir = (0,0,-1000)
  Solid = true
FEATURE [Part::MultiCommon] Common
  Shapes = -> [Extrude_DWire003,Extrude_Rectangle002]
FEATURE [Part::Extrusion] Extrude_Rectangle003  label="Rectangle003_Extrude"
  Base = -> Rectangle003
  Dir = (0,0,-1000)
  Solid = true
FEATURE [Part::Extrusion] Extrude_DWire007  label="DWire007_Extrude"
  Base = -> DWire007
  Dir = (0,0,-1500)
  Solid = true
FEATURE [Part::Extrusion] Extrude_Rectangle004  label="Rectangle004_Extrude"
  Base = -> Rectangle004
  Dir = (0,0,-1500)
  Solid = true
FEATURE [Part::Extrusion] Extrude_Rectangle005  label="Rectangle005_Extrude"
  Base = -> Rectangle005
  Dir = (0,0,-1500)
  Solid = true
FEATURE [Part::MultiCommon] Common001
  Shapes = -> [Extrude_DWire003,Extrude_Rectangle005]
FEATURE [Part::MultiCommon] Common002
  Shapes = -> [Extrude_DWire003,Extrude_Rectangle004]
FEATURE [Part::MultiCommon] Common003
  Shapes = -> [Extrude_DWire003,Extrude_DWire007]
FEATURE [Part::MultiCommon] Common004
  Shapes = -> [Extrude_DWire003,Extrude_Rectangle003]
FEATURE [Part::Part2DObjectPython] Rectangle006  # Draft 2D object (typed FeaturePython)
  ChamferSize = 0
  FilletRadius = 0
  Height = 1760
  Length = -1500
  MakeFace = false
  Placement = pos=(3090,7247.1,3000) rot=(0,0,1;0rad)
FEATURE [Part::Part2DObjectPython] Rectangle007  # Draft 2D object (typed FeaturePython)
  ChamferSize = 0
  FilletRadius = 0
  Height = 1760
  Length = -1320
  MakeFace = false
  Placement = pos=(1520,7247.1,3000) rot=(0,0,1;0rad)
FEATURE [Part::Extrusion] Extrude_Rectangle006  label="Rectangle006_Extrude"
  Base = -> Rectangle006
  Dir = (0,0,-1000)
  Solid = true
FEATURE [Part::Extrusion] Extrude_Rectangle007  label="Rectangle007_Extrude"
  Base = -> Rectangle007
  Dir = (0,0,-1000)
  Solid = true
FEATURE [Part::MultiCommon] Common005
  Shapes = -> [Extrude_DWire003,Extrude_Rectangle006]
FEATURE [Part::MultiCommon] Common006
  Shapes = -> [Extrude_DWire003,Extrude_Rectangle007]
FEATURE [Part::Part2DObjectPython] Line022  # Draft 2D object (typed FeaturePython)
  ChamferSize = 0
  Closed = false
  End = (4290,-70,0)
  FilletRadius = 0
  Length = 4360
  MakeFace = false
  Points = (2) [(-70,-70,0),(4290,-70,0)]
  Start = (-70,-70,0)
FEATURE [Part::Part2DObjectPython] Line023  # Draft 2D object (typed FeaturePython)
  ChamferSize = 0
  Closed = false
  End = (4290,-70,2820)
  FilletRadius = 0
  Length = 4360
  MakeFace = false
  Points = (2) [(-70,-70,2820),(4290,-70,2820)]
  Start = (-70,-70,2820)
FEATURE [Part::Part2DObjectPython] Line024  # Draft 2D object (typed FeaturePython)
  ChamferSize = 0
  Closed = false
  End = (4290,-70,3730)
  FilletRadius = 0
  Length = 4360
  MakeFace = false
  Points = (2) [(-70,-70,3730),(4290,-70,3730)]
  Start = (-70,-70,3730)
FEATURE [Part::Part2DObjectPython] Line025  # Draft 2D object (typed FeaturePython)
  ChamferSize = 0
  Closed = false
  End = (200,-70,4718.17)
  FilletRadius = 0
  Length = 4718.17
  MakeFace = false
  Points = (2) [(200,-70,0),(200,-70,4718.17)]
  Start = (200,-70,0)
FEATURE [Part::Part2DObjectPython] Line026  # Draft 2D object (typed FeaturePython)
  ChamferSize = 0
  Closed = false
  End = (4020,-70,4784.64)
  FilletRadius = 0
  Length = 4784.64
  MakeFace = false
  Points = (2) [(4020,-70,0),(4020,-70,4784.64)]
  Start = (4020,-70,0)
FEATURE [Part::Part2DObjectPython] Line027  # Draft 2D object (typed FeaturePython)
  ChamferSize = 0
  Closed = false
  End = (4020,-70,2820)
  FilletRadius = 0
  Length = 4204.45
  MakeFace = false
  Points = (2) [(-70,-70,3794.32),(4020,-70,2820)]
  Start = (-70,-70,3794.32)
FEATURE [Part::Part2DObjectPython] Line028  # Draft 2D object (typed FeaturePython)
  ChamferSize = 0
  Closed = false
  End = (-70,-70,3845.72)
  FilletRadius = 0
  Length = 4790.4
  MakeFace = false
  Points = (2) [(4590,-70,2735.61),(-70,-70,3845.72)]
  Start = (4590,-70,2735.61)
FEATURE [Part::Part2DObjectPython] DWire008  # Draft 2D object (typed FeaturePython)
  ChamferSize = 0
  Closed = true
  End = (200,-70,3781.4)
  FilletRadius = 0
  Length = 7956.59
  MakeFace = false
  Points = (4) [(200,-70,3730),(4020,-70,2820),(4020,-70,2871.4),(200,-70,3781.4)]
  Start = (200,-70,3730)
FEATURE [Part::Part2DObjectPython] Line029  # Draft 2D object (typed FeaturePython)
  ChamferSize = 0
  Closed = false
  End = (4020,5207,3756.19)
  FilletRadius = 0
  Length = 1576.19
  MakeFace = false
  Points = (2) [(4020,5207,2180),(4020,5207,3756.19)]
  Start = (4020,5207,2180)
FEATURE [Part::Part2DObjectPython] Line030  # Draft 2D object (typed FeaturePython)
  ChamferSize = 0
  Closed = false
  End = (4020,6107,4000)
  FilletRadius = 0
  Length = 4000
  MakeFace = false
  Points = (2) [(4020,6107,0),(4020,6107,4000)]
  Start = (4020,6107,0)
FEATURE [Part::Part2DObjectPython] Line031  # Draft 2D object (typed FeaturePython)
  ChamferSize = 0
  Closed = false
  End = (4020,6467,3756.19)
  FilletRadius = 0
  Length = 1576.19
  MakeFace = false
  Points = (2) [(4020,6467,2180),(4020,6467,3756.19)]
  Start = (4020,6467,2180)
FEATURE [Part::Extrusion] Extrude_DWire008  label="DWire008_Extrude"
  Base = -> DWire008
  Dir = (0,6500,0)
  Solid = true
FEATURE [Part::Part2DObjectPython] Line032  # Draft 2D object (typed FeaturePython)
  ChamferSize = 0
  Closed = false
  End = (-70,6107,4000)
  FilletRadius = 0
  Length = 4090
  MakeFace = false
  Points = (2) [(4020,6107,4000),(-70,6107,4000)]
  Start = (4020,6107,4000)
FEATURE [Part::Part2DObjectPython] Rectangle008  # Draft 2D object (typed FeaturePython)
  ChamferSize = 0
  FilletRadius = 0
  Height = -5907
  Length = 3820
  MakeFace = false
  Placement = pos=(200,6107,4000) rot=(0,0,1;0rad)
FEATURE [Part::Extrusion] Extrude_Rectangle008  label="Rectangle008_Extrude"
  Base = -> Rectangle008
  Dir = (0,0,-2000)
  Solid = true
FEATURE [Part::MultiCommon] Common007
  Shapes = -> [Extrude_DWire008,Extrude_Rectangle008]
FEATURE [Part::Part2DObjectPython] Line033  # Draft 2D object (typed FeaturePython)
  ChamferSize = 0
  Closed = false
  End = (200,6107,2080)
  FilletRadius = 0
  Length = 3820
  MakeFace = false
  Placement = pos=(0,0,2080) rot=(0,0,1;0rad)
  Points = (2) [(4020,6107,0),(200,6107,0)]
  Start = (4020,6107,2080)
FEATURE [Part::FeaturePython] Wall012  label="Wall"  # WARN: FeaturePython — macro-defined, semantics opaque (R4)
  Align = 0
  Base = -> Line033
  Face = 0
  Height = 2000
  Length = 0
  MoveWithHost = false
  Normal = (0,0,0)
  Role = 0
  Width = 360
FEATURE [Part::FeaturePython] Wall010  label="Refend"  # WARN: FeaturePython — macro-defined, semantics opaque (R4)
  Additions = -> [Wall012]
  Align = 0
  Base = -> Line003
  Face = 0
  Height = 4000
  Length = 0
  MoveWithHost = false
  Normal = (0,0,0)
  Role = 0
  Width = 270
FEATURE [Part::Part2DObjectPython] DWire009  # Draft 2D object (typed FeaturePython)
  ChamferSize = 0
  Closed = true
  End = (3090,6467,3000)
  FilletRadius = 0
  Length = 7200.2
  MakeFace = false
  Points = (4) [(200,6467,3000),(200,7177.1,3000),(3090,7177.1,3000),(3090,6467,3000)]
  Start = (200,6467,3000)
FEATURE [Part::Part2DObjectPython] DWire010  # Draft 2D object (typed FeaturePython)
  ChamferSize = 0
  Closed = true
  End = (3160,6467,3000)
  FilletRadius = 0
  Length = 5000.2
  MakeFace = false
  Points = (4) [(3160,8107.1,3000),(4020,8107.1,3000),(4020,6467,3000),(3160,6467,3000)]
  Start = (3160,8107.1,3000)
FEATURE [Part::Extrusion] Extrude_DWire009  label="DWire009_Extrude"
  Base = -> DWire009
  Dir = (0,0,-2000)
  Solid = true
FEATURE [Part::Extrusion] Extrude_DWire010  label="DWire010_Extrude"
  Base = -> DWire010
  Dir = (0,0,-2000)
  Solid = true
FEATURE [Part::MultiCommon] Common008
  Shapes = -> [Extrude_DWire009,Extrude_DWire003]
FEATURE [Part::MultiCommon] Common009
  Shapes = -> [Extrude_DWire010,Extrude_DWire003]
FEATURE [Part::Part2DObjectPython] Line034  # Draft 2D object (typed FeaturePython)
  ChamferSize = 0
  Closed = false
  End = (-70,-70,3948.52)
  FilletRadius = 0
  Length = 4790.4
  MakeFace = false
  Points = (2) [(4590,-70,2838.41),(-70,-70,3948.52)]
  Start = (4590,-70,2838.41)
FEATURE [Part::Part2DObjectPython] Line035  # Draft 2D object (typed FeaturePython)
  ChamferSize = 0
  Closed = false
  End = (10950,5877.1,2033.05)
  FilletRadius = 0
  Length = 3195.73
  MakeFace = false
  Points = (2) [(10950,9007.1,2677.89),(10950,5877.1,2033.05)]
  Start = (10950,9007.1,2677.89)
FEATURE [Part::Part2DObjectPython] Line036  # Draft 2D object (typed FeaturePython)
  ChamferSize = 0
  Closed = false
  End = (10950,9277.1,2835.61)
  FilletRadius = 0
  Length = 3747.07
  MakeFace = false
  Points = (2) [(10950,5607.1,2079.53),(10950,9277.1,2835.61)]
  Start = (10950,5607.1,2079.53)
FEATURE [Part::Part2DObjectPython] DWire011  # Draft 2D object (typed FeaturePython)
  ChamferSize = 0
  Closed = true
  End = (10950,5607.1,4000)
  FilletRadius = 0
  Length = 10501.9
  MakeFace = true
  Points = (4) [(10950,5607.1,2079.53),(10950,9277.1,2835.61),(10950,9277.1,4000),(10950,5607.1,4000)]
  Start = (10950,5607.1,2079.53)
FEATURE [Part::Extrusion] Extrude_DWire011  label="DWire011_Extrude"
  Base = -> DWire011
  Dir = (-11020,0,0)
  Solid = true
FEATURE [Part::Part2DObjectPython] Rectangle009  # Draft 2D object (typed FeaturePython)
  ChamferSize = 0
  FilletRadius = 0
  Height = -6537
  Length = -4360
  MakeFace = true
  Placement = pos=(-70,-70,4000) rot=(0,0,1;3.14159rad)
FEATURE [Part::Extrusion] Extrude_Rectangle009  label="Rectangle009_Extrude"
  Base = -> Rectangle009
  Dir = (0,0,-3000)
  Solid = true
FEATURE [Part::Cut] Cut
  Base = -> Extrude_DWire011
  Tool = -> Extrude_Rectangle009
FEATURE [Part::FeaturePython] Wall  label="Cloisons002"  # WARN: FeaturePython — macro-defined, semantics opaque (R4)
  Additions = -> [Wall001,Wall002,Wall005,Wall004,Wall003]
  Align = 1
  Base = -> TraceDuMur
  Face = 0
  Height = 3000
  Length = 0
  MoveWithHost = false
  Normal = (0,0,0)
  Role = 0
  Subtractions = -> [Window005,Window006,Window009,Window010,Window011,Cut]
  Width = 70
FEATURE [Part::FeaturePython] Wall006  label="Cloisons001"  # WARN: FeaturePython — macro-defined, semantics opaque (R4)
  Additions = -> [Wall007,Wall008]
  Align = 0
  Base = -> Line
  Face = 0
  Height = 3000
  Length = 0
  MoveWithHost = false
  Normal = (0,0,0)
  Role = 0
  Subtractions = -> [Window007,Window008,Cut]
  Width = 70
FEATURE [Part::Part2DObjectPython] Line037  # Draft 2D object (typed FeaturePython)
  ChamferSize = 0
  Closed = false
  End = (4290,6467,4000)
  FilletRadius = 0
  Length = 270
  MakeFace = false
  Points = (2) [(4020,6467,4000),(4290,6467,4000)]
  Start = (4020,6467,4000)
FEATURE [Part::Part2DObjectPython] DWire012  # Draft 2D object (typed FeaturePython)
  ChamferSize = 0
  Closed = true
  End = (-70,-70,4899.23)
  FilletRadius = 0
  Length = 11782.1
  MakeFace = false
  Points = (4) [(-70,-70,3948.52),(4290,-70,2909.88),(4290,-70,4899.23),(-70,-70,4899.23)]
  Start = (-70,-70,3948.52)
FEATURE [Part::Extrusion] Extrude_DWire012  label="DWire012_Extrude"
  Base = -> DWire012
  Dir = (0,6537,0)
  Solid = true
FEATURE [Part::FeaturePython] Wall009  label="MursExtérieur"  # WARN: FeaturePython — macro-defined, semantics opaque (R4)
  Additions = -> [Wall010]
  Align = 0
  Base = -> DWire
  Face = 0
  Height = 4000
  Length = 0
  MoveWithHost = false
  Normal = (0,0,0)
  Role = 0
  Subtractions = -> [Window,Window001,Window002,Window003,Window004,Cut,Extrude_DWire012]
  Width = 270
FEATURE [Part::Part2DObjectPython] Line038  # Draft 2D object (typed FeaturePython)
  ChamferSize = 0
  Closed = false
  End = (-70,-70,4051.32)
  FilletRadius = 0
  Length = 4790.4
  MakeFace = false
  Points = (2) [(4590,-70,2941.21),(-70,-70,4051.32)]
  Start = (4590,-70,2941.21)
FEATURE [Part::Part2DObjectPython] Line039  # Draft 2D object (typed FeaturePython)
  ChamferSize = 0
  Closed = false
  End = (4290,-70,4784.64)
  FilletRadius = 0
  Length = 4784.64
  MakeFace = false
  Points = (2) [(4290,-70,0),(4290,-70,4784.64)]
  Start = (4290,-70,0)
FEATURE [Part::Part2DObjectPython] Line040  # Draft 2D object (typed FeaturePython)
  ChamferSize = 0
  Closed = false
  End = (4590,-70,4784.64)
  FilletRadius = 0
  Length = 4784.64
  MakeFace = false
  Points = (2) [(4590,-70,0),(4590,-70,4784.64)]
  Start = (4590,-70,0)
FEATURE [Part::Part2DObjectPython] DWire013  # Draft 2D object (typed FeaturePython)
  ChamferSize = 0
  Closed = true
  End = (4590,-70,2838.41)
  FilletRadius = 0
  Length = 9786.4
  MakeFace = true
  Points = (4) [(-70,-70,3948.52),(-70,-70,3845.72),(4590,-70,2735.61),(4590,-70,2838.41)]
  Start = (-70,-70,3948.52)
FEATURE [Part::FeaturePython] Structure003  # WARN: FeaturePython — macro-defined, semantics opaque (R4)
  Base = -> DWire013
  Height = 80
  Length = 0
  MoveWithHost = false
  Nodes = (2) [(2260,-70,3342.07),(2260,10,3342.07)]
  Normal = (0,1,0)
  Role = 0
  Width = 100
FEATURE [Part::FeaturePython] Array  # Draft array (typed FeaturePython)
  Angle = 360
  ArrayType = 0
  Axis = (0,0,1)
  Base = -> Structure003
  Center = (0,0,0)
  Fuse = false
  IntervalAxis = (0,0,0)
  IntervalX = (1,0,0)
  IntervalY = (0,496,0)
  IntervalZ = (0,0,0)
  NumberPolar = 1
  NumberX = 1
  NumberY = 14
  NumberZ = 1
FEATURE [Part::FeaturePython] Structure004  # WARN: FeaturePython — macro-defined, semantics opaque (R4)
  Height = 200
  Length = 6107
  MoveWithHost = false
  Nodes = (2) [(0,0,0),(6107,0,0)]
  Normal = (0,0,0)
  Placement = pos=(2416.83,140,3150.51) rot=(0.115878,0.115878,0.986481;1.58441rad)
  Role = 0
  Width = 100
FEATURE [Part::FeaturePython] TimberBeam001  # WARN: FeaturePython — macro-defined, semantics opaque (R4)
  Base = -> Structure004
  Height = 200
  Length = 6107
  Moise = false
  MoveWithHost = false
  Normal = (0,0,0)
  Placement = pos=(2416.83,140,3150.51) rot=(0.115878,0.115878,0.986481;1.58441rad)
  Preset = 0
  Role = 0
  Width = 100
FEATURE [Part::Feature] TimberBeam001001  label="TimberBeam002"
  Placement = pos=(2416.83,140,3150.51) rot=(0.115878,0.115878,0.986481;1.58441rad)
  shape: bbox 143.6 x 6107 x 217.7 mm, 6 faces (baked)
FEATURE [Part::Cut] Cut001
  Base = -> Common007
  Tool = -> TimberBeam001001
FEATURE [Part::FeaturePython] Structure005  # WARN: FeaturePython — macro-defined, semantics opaque (R4)
  Height = 220
  Length = 3549
  MoveWithHost = false
  Nodes = (2) [(0,0,0),(3549,0,0)]
  Normal = (0,0,0)
  Placement = pos=(151.645,3357,3474.25) rot=(0,1,0;0.233864rad)
  Role = 0
  Width = 90
FEATURE [Part::FeaturePython] TimberMachiningCut  # WARN: FeaturePython — macro-defined, semantics opaque (R4)
  Beam = -> Structure005
  CutPlane = -> TimberBeam [Face2]
FEATURE [Part::FeaturePython] TimberBeam001002  # WARN: FeaturePython — macro-defined, semantics opaque (R4)
  Base = -> Structure005
  Height = 220
  Length = 3549
  Moise = false
  MoveWithHost = false
  Normal = (0,0,0)
  Placement = pos=(151.645,3357,3474.25) rot=(0,1,0;0.233864rad)
  Preset = 0
  Role = 0
  Subtractions = -> [TimberMachiningCut]
  Width = 90
FEATURE [App::DocumentObjectGroup] Groupe001  label="ObjetsConstruction"
  Group = -> [Sketch001,Sketch011]
FEATURE [Part::Part2DObjectPython] DWire014  # Draft 2D object (typed FeaturePython)
  ChamferSize = 0
  Closed = true
  End = (4590,-70,2941.21)
  FilletRadius = 0
  Length = 9786.4
  MakeFace = true
  Points = (4) [(-70,-70,4051.32),(-70,-70,3948.52),(4590,-70,2838.41),(4590,-70,2941.21)]
  Start = (-70,-70,4051.32)
FEATURE [Part::Part2DObjectPython] Line041  # Draft 2D object (typed FeaturePython)
  ChamferSize = 0
  Closed = false
  End = (10950,5557.1,3000)
  FilletRadius = 0
  Length = 3000
  MakeFace = false
  Points = (2) [(10950,5557.1,0),(10950,5557.1,3000)]
  Start = (10950,5557.1,0)
FEATURE [Part::Part2DObjectPython] Line042  # Draft 2D object (typed FeaturePython)
  ChamferSize = 0
  Closed = false
  End = (10950,9277.1,3000)
  FilletRadius = 0
  Length = 3000
  MakeFace = false
  Points = (2) [(10950,9277.1,0),(10950,9277.1,3000)]
  Start = (10950,9277.1,0)
FEATURE [Part::Part2DObjectPython] Line043  # Draft 2D object (typed FeaturePython)
  ChamferSize = 0
  Closed = false
  End = (10950,9256.92,2831.46)
  FilletRadius = 0
  Length = 3798.12
  MakeFace = false
  Points = (2) [(10950,5536.92,2065.07),(10950,9256.92,2831.46)]
  Start = (10950,5536.92,2065.07)
FEATURE [Part::Part2DObjectPython] DWire015  # Draft 2D object (typed FeaturePython)
  ChamferSize = 0
  Closed = true
  End = (10950,9277.1,2835.61)
  FilletRadius = 0
  Length = 7800.45
  MakeFace = false
  Points = (4) [(10950,5557.1,2069.22),(10950,5557.1,1967.12),(10950,9277.1,2733.51),(10950,9277.1,2835.61)]
  Start = (10950,5557.1,2069.22)
FEATURE [Part::FeaturePython] Structure007  # WARN: FeaturePython — macro-defined, semantics opaque (R4)
  Base = -> DWire015
  Height = 80
  Length = 0
  MoveWithHost = false
  Normal = (1,0,0)
  Placement = pos=(-6660,0,0) rot=(0,0,1;0rad)
  Role = 0
  Width = 100
FEATURE [App::FeaturePython] Axes  # WARN: FeaturePython — macro-defined, semantics opaque (R4)
  Angles = [0,0,0,0,0,0,0,0,0,0,0,0,0,0]
  Distances = [0,500,500,500,500,500,500,500,500,500,500,500,500,500]
  Length = 3000
FEATURE [Part::FeaturePython] StructuralSystem  # WARN: FeaturePython — macro-defined, semantics opaque (R4)
  Axes = -> [Axes]
  Base = -> Structure007
  MoveWithHost = false
  Role = 0
FEATURE [Part::Part2DObjectPython] Line044  # Draft 2D object (typed FeaturePython)
  ChamferSize = 0
  Closed = false
  End = (10950,6467,0)
  FilletRadius = 0
  Length = 2909.88
  MakeFace = false
  Points = (2) [(10950,6467,2909.88),(10950,6467,0)]
  Start = (10950,6467,2909.88)
FEATURE [Part::Part2DObjectPython] DWire016  # Draft 2D object (typed FeaturePython)
  ChamferSize = 0
  Closed = true
  End = (10950,6467,2256.68)
  FilletRadius = 0
  Length = 5942.43
  MakeFace = false
  Points = (4) [(10950,6467,2154.58),(10950,9277.1,2733.51),(10950,9277.1,2835.61),(10950,6467,2256.68)]
  Start = (10950,6467,2154.58)
FEATURE [Part::FeaturePython] Structure008  # WARN: FeaturePython — macro-defined, semantics opaque (R4)
  Base = -> DWire016
  Height = 80
  Length = 0
  MoveWithHost = false
  Normal = (1,0,0)
  Placement = pos=(-11020,0,0) rot=(0,0,1;0rad)
  Role = 0
  Width = 100
FEATURE [App::FeaturePython] Axes001  # WARN: FeaturePython — macro-defined, semantics opaque (R4)
  Angles = [0,0,0,0,0,0,0,0,0,0]
  Distances = [0,500,500,500,500,500,500,500,500,280]
  Length = 3000
FEATURE [Part::Part2DObjectPython] Line045  # Draft 2D object (typed FeaturePython)
  ChamferSize = 0
  Closed = false
  End = (10950,5516.74,2163.01)
  FilletRadius = 0
  Length = 3839.33
  MakeFace = false
  Points = (2) [(10950,9277.1,2937.71),(10950,5516.74,2163.01)]
  Start = (10950,9277.1,2937.71)
FEATURE [App::DocumentObjectGroup] Construction
  Group = -> [Line004,Line005,Line006,Line007,Line008,Line009,Line010,Line011,Line012,Line014,Line013,Line015,Line016,Line017,Line018,Line019,Line020,Line021,Line022,Line023,Line024,Line025,Line026,Line027,Line028,Line029,Line030,Line031,Line032,Line034,Line035,Line036,Line037,Line038,Line040,Line039,Line041,Line042,Line043,Line044,Line045]
FEATURE [Part::Part2DObjectPython] DWire017  # Draft 2D object (typed FeaturePython)
  ChamferSize = 0
  Closed = true
  End = (10950,9277.1,2937.71)
  FilletRadius = 0
  Length = 5942.43
  MakeFace = false
  Points = (4) [(10950,6467,2358.78),(10950,6467,2256.68),(10950,9277.1,2835.61),(10950,9277.1,2937.71)]
  Start = (10950,6467,2358.78)
FEATURE [Part::FeaturePython] Structure009  # WARN: FeaturePython — macro-defined, semantics opaque (R4)
  Base = -> DWire017
  Height = 4360
  Length = 0
  MoveWithHost = false
  Normal = (1,0,0)
  Placement = pos=(-11020,0,0) rot=(0,0,1;0rad)
  Role = 0
  Width = 100
FEATURE [Part::Part2DObjectPython] DWire018  # Draft 2D object (typed FeaturePython)
  ChamferSize = 0
  Closed = true
  End = (10950,9277.1,2937.71)
  FilletRadius = 0
  Length = 7800.45
  MakeFace = false
  Points = (4) [(10950,5557.1,2171.32),(10950,5557.1,2069.22),(10950,9277.1,2835.61),(10950,9277.1,2937.71)]
  Start = (10950,5557.1,2171.32)
FEATURE [Sketcher::SketchObject] Sketch016
  Placement = pos=(1904.61,4196.71,3580.92) rot=(0.115878,0.115878,0.986481;1.58441rad)
  sketch-geometry (8):
    g0: LineSegment StartX=0 StartY=0 StartZ=0 EndX=800 EndY=0 EndZ=0
    g1: LineSegment StartX=800 StartY=0 StartZ=0 EndX=800 EndY=900 EndZ=0
    g2: LineSegment StartX=800 StartY=900 StartZ=0 EndX=0 EndY=900 EndZ=0
    g3: LineSegment StartX=0 StartY=900 StartZ=0 EndX=0 EndY=0 EndZ=0
    g4: LineSegment StartX=100 StartY=100 StartZ=0 EndX=700 EndY=100 EndZ=0
    g5: LineSegment StartX=700 StartY=100 StartZ=0 EndX=700 EndY=800 EndZ=0
    g6: LineSegment StartX=700 StartY=800 StartZ=0 EndX=100 EndY=800 EndZ=0
    g7: LineSegment StartX=100 StartY=800 StartZ=0 EndX=100 EndY=100 EndZ=0
  constraints (23):
    c: Coincident(g0,g1)
    c: Coincident(g1,g2)
    c: Coincident(g2,g3)
    c: Coincident(g3,g0)
    c: Horizontal(g0)
    c: Horizontal(g2)
    c: Vertical(g1)
    c: Vertical(g3)
    c: Coincident(g4,g5)
    c: Coincident(g5,g6)
    c: Coincident(g6,g7)
    c: Coincident(g7,g4)
    c: Horizontal(g4)
    c: Horizontal(g6)
    c: Vertical(g5)
    c: Vertical(g7)
    c: DistanceY(g1) = 900
    c: DistanceX(g0) = 800
    c: DistanceY(g6,g2) = 100
    c: DistanceX(g2,g6) = 100
    c: DistanceX(g4,g0) = 100
    c: DistanceY(g0,g4) = 100
    c: Coincident(g0,g-1)
FEATURE [Part::FeaturePython] Window012  label="Window"  # WARN: FeaturePython — macro-defined, semantics opaque (R4)
  Base = -> Sketch016
  Height = 900
  HoleDepth = 0
  MoveWithHost = true
  Normal = (-0.231735,0,-0.972779)
  Preset = 1
  Role = 0
  Width = 800
  WindowParts = OuterFrame | Frame | Wire0,Wire1 | 100.0 | 0.0 | Glass | Glass panel | Wire1 | 10.0 | 50.0
FEATURE [Part::FeaturePython] Structure006  # WARN: FeaturePython — macro-defined, semantics opaque (R4)
  Base = -> DWire014
  Height = 6537
  Length = 0
  MoveWithHost = false
  Nodes = (2) [(2260,-70,3444.86),(2260,6467,3444.86)]
  Normal = (0,1,0)
  Role = 0
  Subtractions = -> [Window012]
  Width = 100
FEATURE [Sketcher::SketchObject] Sketch017
  Placement = pos=(1992.11,7739.7,2620.98) rot=(1,0,0;0.203176rad)
  sketch-geometry (8):
    g0: LineSegment StartX=0 StartY=0 StartZ=0 EndX=800 EndY=0 EndZ=0
    g1: LineSegment StartX=800 StartY=0 StartZ=0 EndX=800 EndY=900 EndZ=0
    g2: LineSegment StartX=800 StartY=900 StartZ=0 EndX=0 EndY=900 EndZ=0
    g3: LineSegment StartX=0 StartY=900 StartZ=0 EndX=0 EndY=0 EndZ=0
    g4: LineSegment StartX=100 StartY=100 StartZ=0 EndX=700 EndY=100 EndZ=0
    g5: LineSegment StartX=700 StartY=100 StartZ=0 EndX=700 EndY=800 EndZ=0
    g6: LineSegment StartX=700 StartY=800 StartZ=0 EndX=100 EndY=800 EndZ=0
    g7: LineSegment StartX=100 StartY=800 StartZ=0 EndX=100 EndY=100 EndZ=0
  constraints (23):
    c: Coincident(g0,g1)
    c: Coincident(g1,g2)
    c: Coincident(g2,g3)
    c: Coincident(g3,g0)
    c: Horizontal(g0)
    c: Horizontal(g2)
    c: Vertical(g1)
    c: Vertical(g3)
    c: Coincident(g4,g5)
    c: Coincident(g5,g6)
    c: Coincident(g6,g7)
    c: Coincident(g7,g4)
    c: Horizontal(g4)
    c: Horizontal(g6)
    c: Vertical(g5)
    c: Vertical(g7)
    c: DistanceY(g1) = 900
    c: DistanceX(g0) = 800
    c: DistanceY(g6,g2) = 100
    c: DistanceX(g2,g6) = 100
    c: DistanceX(g4,g0) = 100
    c: DistanceY(g0,g4) = 100
    c: Coincident(g0,g-1)
FEATURE [Part::FeaturePython] Window013  label="Window001"  # WARN: FeaturePython — macro-defined, semantics opaque (R4)
  Base = -> Sketch017
  Height = 900
  HoleDepth = 0
  MoveWithHost = true
  Normal = (0,0.201781,-0.979431)
  Preset = 1
  Role = 0
  Width = 800
  WindowParts = OuterFrame | Frame | Wire0,Wire1 | 100.0 | 0.0 | Glass | Glass panel | Wire1 | 10.0 | 50.0
FEATURE [Part::FeaturePython] StructuralSystem001  # WARN: FeaturePython — macro-defined, semantics opaque (R4)
  Axes = -> [Axes001]
  Base = -> Structure008
  MoveWithHost = false
  Role = 0
  Subtractions = -> [Window013]
FEATURE [Part::FeaturePython] Structure010  # WARN: FeaturePython — macro-defined, semantics opaque (R4)
  Additions = -> [Structure009]
  Base = -> DWire018
  Height = 6660
  Length = 0
  MoveWithHost = false
  Normal = (1,0,0)
  Placement = pos=(-6660,0,0) rot=(0,0,1;0rad)
  Role = 0
  Subtractions = -> [Window013]
  Width = 100
FEATURE [App::DocumentObjectGroupPython] Floor004  label="Toiture"  # scripted group (container) (typed FeaturePython)
  Group = -> [Structure010,Structure006]
  Height = 0
FEATURE [Part::Part2DObjectPython] DWire019  label="Sol"  # Draft 2D object (typed FeaturePython)
  ChamferSize = 0
  Closed = true
  End = (-70,9277.1,0)
  FilletRadius = 0
  Length = 40734.2
  MakeFace = true
  Points = (6) [(-70,-70,0),(4290,-70,0),(4290,5607.1,0),(10950,5607.1,0),(10950,9277.1,0),(-70,9277.1,0)]
  Start = (-70,-70,0)
FEATURE [Part::FeaturePython] Structure011  # WARN: FeaturePython — macro-defined, semantics opaque (R4)
  Base = -> Array
  Height = 1000
  Length = 0
  MoveWithHost = false
  Normal = (0,0,0)
  Role = 0
  Subtractions = -> [Window012]
  Width = 100
FEATURE [App::DocumentObjectGroupPython] Floor002  label="Charpente"  # scripted group (container) (typed FeaturePython)
  Group = -> [TimberBeam001,TimberBeam001002,TimberBeam,StructuralSystem001,Axes001,StructuralSystem,Axes,Structure011]
  Height = 0
FEATURE [Part::FeaturePython] Structure012  # WARN: FeaturePython — macro-defined, semantics opaque (R4)
  Base = -> Cut001
  Height = 1000
  Length = 0
  MoveWithHost = false
  Normal = (0,0,0)
  Role = 0
  Subtractions = -> [Window012]
  Width = 100
FEATURE [Part::FeaturePython] Structure013  # WARN: FeaturePython — macro-defined, semantics opaque (R4)
  Base = -> Common005
  Height = 1000
  Length = 0
  MoveWithHost = false
  Normal = (0,0,0)
  Role = 0
  Subtractions = -> [Window013]
  Width = 100
FEATURE [Part::FeaturePython] Structure014  # WARN: FeaturePython — macro-defined, semantics opaque (R4)
  Base = -> Common
  Height = 1000
  Length = 0
  MoveWithHost = false
  Normal = (0,0,0)
  Role = 0
  Width = 100
FEATURE [Part::FeaturePython] Structure015  # WARN: FeaturePython — macro-defined, semantics opaque (R4)
  Base = -> Common001
  Height = 1000
  Length = 0
  MoveWithHost = false
  Normal = (0,0,0)
  Role = 0
  Width = 100
FEATURE [Part::FeaturePython] Structure016  # WARN: FeaturePython — macro-defined, semantics opaque (R4)
  Base = -> Common006
  Height = 1000
  Length = 0
  MoveWithHost = false
  Normal = (0,0,0)
  Role = 0
  Width = 100
FEATURE [Part::FeaturePython] Structure017  # WARN: FeaturePython — macro-defined, semantics opaque (R4)
  Base = -> Common002
  Height = 1000
  Length = 0
  MoveWithHost = false
  Normal = (0,0,0)
  Role = 0
  Width = 100
FEATURE [Part::FeaturePython] Structure018  # WARN: FeaturePython — macro-defined, semantics opaque (R4)
  Base = -> Common009
  Height = 1000
  Length = 0
  MoveWithHost = false
  Normal = (0,0,0)
  Role = 0
  Width = 100
FEATURE [Part::FeaturePython] Structure019  # WARN: FeaturePython — macro-defined, semantics opaque (R4)
  Base = -> Common008
  Height = 1000
  Length = 0
  MoveWithHost = false
  Normal = (0,0,0)
  Role = 0
  Width = 100
FEATURE [Part::FeaturePython] Structure020  # WARN: FeaturePython — macro-defined, semantics opaque (R4)
  Base = -> Common003
  Height = 1000
  Length = 0
  MoveWithHost = false
  Normal = (0,0,0)
  Role = 0
  Width = 100
FEATURE [Part::FeaturePython] Structure021  # WARN: FeaturePython — macro-defined, semantics opaque (R4)
  Base = -> Common004
  Height = 1000
  Length = 0
  MoveWithHost = false
  Normal = (0,0,0)
  Role = 0
  Width = 100
FEATURE [App::DocumentObjectGroupPython] Floor  label="Plafonds"  # scripted group (container) (typed FeaturePython)
  Group = -> [Structure001,Structure013,Structure012,Structure014,Structure015,Structure016,Structure017,Structure018,Structure019,Structure020,Structure021]
  Height = 0
FEATURE [Part::FeaturePython] Structure022  label="Conduit poele à bois"  # WARN: FeaturePython — macro-defined, semantics opaque (R4)
  Base = -> Sweep
  Height = 1000
  Length = 0
  MoveWithHost = false
  Normal = (0,0,0)
  Role = 0
  Width = 100
FEATURE [App::DocumentObjectGroupPython] Floor001  label="Mobilier"  # scripted group (container) (typed FeaturePython)
  Group = -> [Equipment,Equipment001,Equipment002,Equipment003,Equipment004,Equipment005,Equipment006,Rectangle,Equipment007,Equipment008,Equipment009,Equipment010,Equipment012,Equipment013,Equipment014,Equipment015,Equipment016,Equipment017,Equipment018,Equipment019,Equipment020,Equipment021,Equipment022,Equipment023,Equipment024,Equipment025,Equipment026,Equipment027,Equipment028,Equipment029,Equipment030,+1 more]
  Height = 0
FEATURE [Part::FeaturePython] Structure023  label="Structure022"  # WARN: FeaturePython — macro-defined, semantics opaque (R4)
  Base = -> Extrusion001
  Height = 1000
  Length = 0
  MoveWithHost = false
  Normal = (0,0,0)
  Role = 0
  Width = 100
FEATURE [App::DocumentObjectGroupPython] Floor003  label="Cloisons"  # scripted group (container) (typed FeaturePython)
  Group = -> [Wall,Wall006,Wall011,Structure002,Structure023]
  Height = 0
